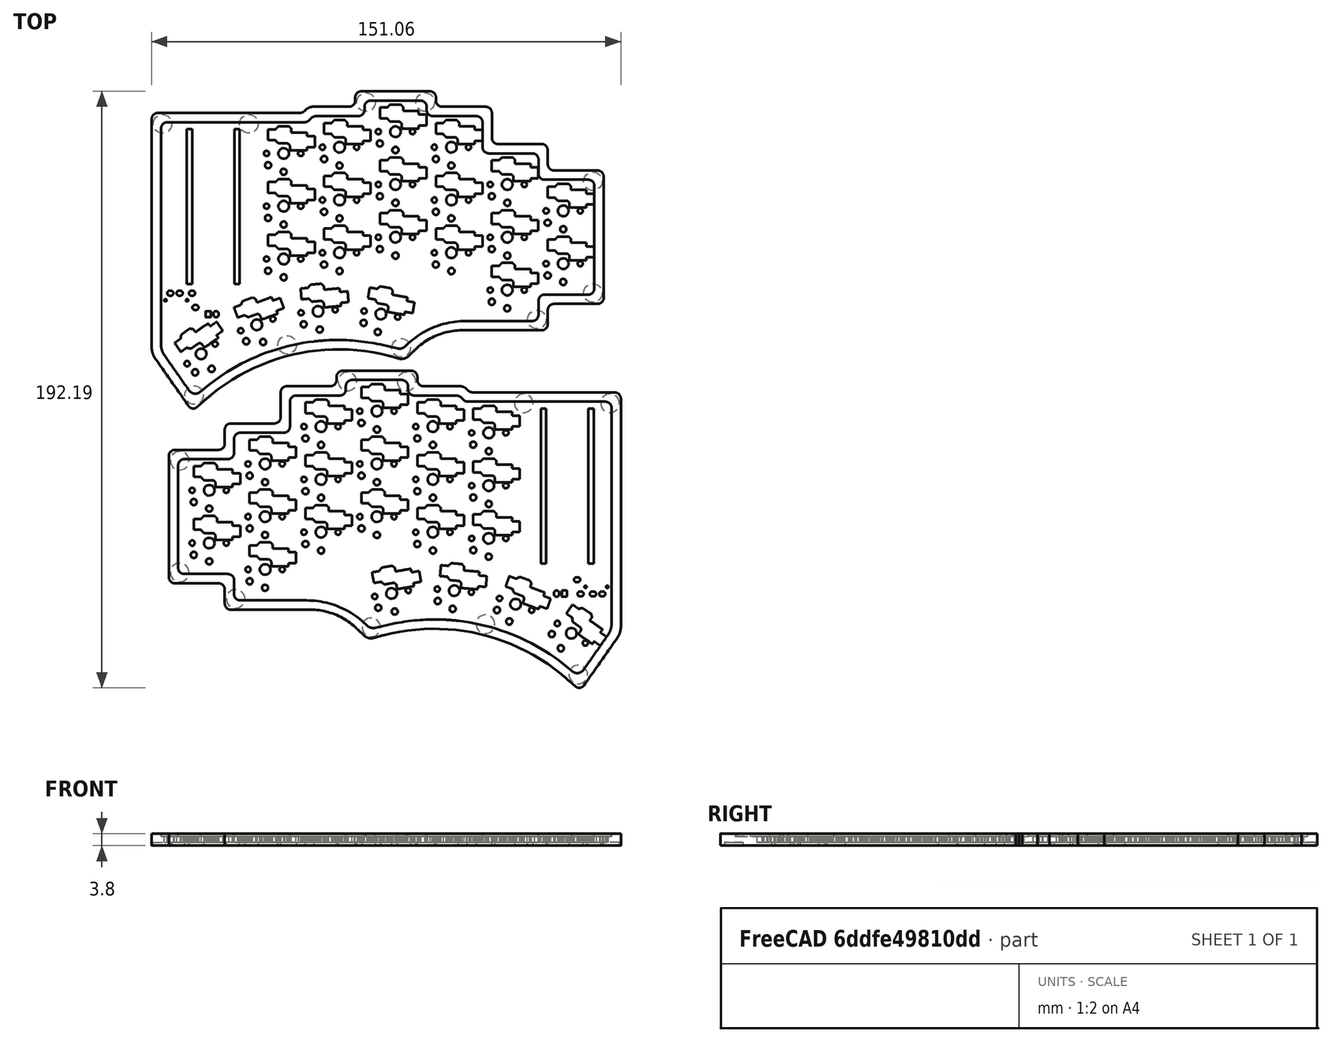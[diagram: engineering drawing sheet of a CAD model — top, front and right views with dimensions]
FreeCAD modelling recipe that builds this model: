
FCSTD DOCUMENT  (FreeCAD 0.21R33771 (Git))
Label: case
License: All rights reserved
LicenseURL: http://en.wikipedia.org/wiki/All_rights_reserved
objects: Part::Feature×296, Part::Extrusion×296, Part::MultiFuse×4, Part::FeaturePython×2, Part::Mirroring×1
note: 599 computed .brp shape members not serialized (recipe doc carries the construction recipe); baked Part::Feature solids carry a one-line shape summary decoded from their .brp

FEATURE [Part::Feature] path44149_5_3
  shape: bbox 145.5 x 102.4 x 2e-07 mm, 0 faces, 0 solids (baked)
FEATURE [Part::Extrusion] Extrude  label="bounds_left"
  Base = -> path44149_5_3
  Dir = (0,0,1)
  DirMode = 0
  FaceMakerClass = Part::FaceMakerBullseye
  LengthFwd = 3.8
  LengthRev = 0
  Solid = true
  Symmetric = false
FEATURE [Part::Feature] path44149_5_1
  shape: bbox 139.5 x 94.73 x 2e-07 mm, 0 faces, 0 solids (baked)
FEATURE [Part::Extrusion] Extrude001  label="inner_left"
  Base = -> path44149_5_1
  Dir = (0,0,1)
  DirMode = 0
  FaceMakerClass = Part::FaceMakerBullseye
  LengthFwd = 0.8
  LengthRev = 0
  Placement = pos=(0,0,3) rot=(0,0,1;0rad)
  Solid = true
  Symmetric = false
FEATURE [Part::Feature] path9
  Placement = pos=(71.4721,-85.7664,0) rot=(0,0,1;0rad)
  shape: bbox 6.624 x 7.244 x 2e-07 mm, 0 faces, 0 solids (baked)
FEATURE [Part::Feature] path9_9
  Placement = pos=(71.4721,-121.766,0) rot=(0,0,1;0rad)
  shape: bbox 6.624 x 7.244 x 2e-07 mm, 0 faces, 0 solids (baked)
FEATURE [Part::Feature] path9_92_7_9
  Placement = pos=(125.472,-60.2664,0) rot=(0,0,1;0rad)
  shape: bbox 6.624 x 7.244 x 2e-07 mm, 0 faces, 0 solids (baked)
FEATURE [Part::Feature] path9_92_7_9_9
  Placement = pos=(144.472,-60.2664,0) rot=(0,0,1;0rad)
  shape: bbox 6.624 x 7.244 x 2e-07 mm, 0 faces, 0 solids (baked)
FEATURE [Part::Feature] path9_92_7_9_9_4
  Placement = pos=(210.001,-67.2664,0) rot=(0,0,1;0rad)
  shape: bbox 6.624 x 7.244 x 2e-07 mm, 0 faces, 0 solids (baked)
FEATURE [Part::Feature] path9_9_5
  Placement = pos=(89.4721,-130.266,0) rot=(0,0,1;0rad)
  shape: bbox 6.624 x 7.244 x 2e-07 mm, 0 faces, 0 solids (baked)
FEATURE [Part::Feature] path9_92_7_9_9_4_4_8_2
  Placement = pos=(199.796,-154.63,0) rot=(0,0,1;0rad)
  shape: bbox 6.624 x 7.244 x 2e-07 mm, 0 faces, 0 solids (baked)
FEATURE [Part::Feature] path9_92_7_9_9_4_4_8_2_4
  Placement = pos=(133.155,-139.413,0) rot=(0,0,1;0rad)
  shape: bbox 6.624 x 7.244 x 2e-07 mm, 0 faces, 0 solids (baked)
FEATURE [Part::Feature] path9_92_7_9_9_4_4_8_2_4_6
  Placement = pos=(169.885,-138.433,0) rot=(0,0,1;0rad)
  shape: bbox 6.624 x 7.244 x 2e-07 mm, 0 faces, 0 solids (baked)
FEATURE [Part::Feature] path9_92_7_9_9_4_4_8_2_4_0
  Placement = pos=(182.228,-67.2664,0) rot=(0,0,1;0rad)
  shape: bbox 6.624 x 7.244 x 2e-07 mm, 0 faces, 0 solids (baked)
FEATURE [Part::Extrusion] Extrude002
  Base = -> path9
  Dir = (0,0,1)
  DirMode = 0
  FaceMakerClass = Part::FaceMakerBullseye
  LengthFwd = 1
  LengthRev = 0
  Solid = true
  Symmetric = false
FEATURE [Part::Extrusion] Extrude003
  Base = -> path9_9
  Dir = (0,0,1)
  DirMode = 0
  FaceMakerClass = Part::FaceMakerBullseye
  LengthFwd = 1
  LengthRev = 0
  Solid = true
  Symmetric = false
FEATURE [Part::Extrusion] Extrude004
  Base = -> path9_92_7_9
  Dir = (0,0,1)
  DirMode = 0
  FaceMakerClass = Part::FaceMakerBullseye
  LengthFwd = 1
  LengthRev = 0
  Solid = true
  Symmetric = false
FEATURE [Part::Extrusion] Extrude005
  Base = -> path9_92_7_9_9
  Dir = (0,0,1)
  DirMode = 0
  FaceMakerClass = Part::FaceMakerBullseye
  LengthFwd = 1
  LengthRev = 0
  Solid = true
  Symmetric = false
FEATURE [Part::Extrusion] Extrude006
  Base = -> path9_92_7_9_9_4
  Dir = (0,0,1)
  DirMode = 0
  FaceMakerClass = Part::FaceMakerBullseye
  LengthFwd = 1
  LengthRev = 0
  Solid = true
  Symmetric = false
FEATURE [Part::Extrusion] Extrude007
  Base = -> path9_9_5
  Dir = (0,0,1)
  DirMode = 0
  FaceMakerClass = Part::FaceMakerBullseye
  LengthFwd = 1
  LengthRev = 0
  Solid = true
  Symmetric = false
FEATURE [Part::Extrusion] Extrude008
  Base = -> path9_92_7_9_9_4_4_8_2
  Dir = (0,0,1)
  DirMode = 0
  FaceMakerClass = Part::FaceMakerBullseye
  LengthFwd = 1
  LengthRev = 0
  Solid = true
  Symmetric = false
FEATURE [Part::Extrusion] Extrude009
  Base = -> path9_92_7_9_9_4_4_8_2_4
  Dir = (0,0,1)
  DirMode = 0
  FaceMakerClass = Part::FaceMakerBullseye
  LengthFwd = 1
  LengthRev = 0
  Solid = true
  Symmetric = false
FEATURE [Part::Extrusion] Extrude010
  Base = -> path9_92_7_9_9_4_4_8_2_4_6
  Dir = (0,0,1)
  DirMode = 0
  FaceMakerClass = Part::FaceMakerBullseye
  LengthFwd = 1
  LengthRev = 0
  Solid = true
  Symmetric = false
FEATURE [Part::Extrusion] Extrude011
  Base = -> path9_92_7_9_9_4_4_8_2_4_0
  Dir = (0,0,1)
  DirMode = 0
  FaceMakerClass = Part::FaceMakerBullseye
  LengthFwd = 1
  LengthRev = 0
  Solid = true
  Symmetric = false
FEATURE [Part::MultiFuse] Fusion  label="feet_left"
  Shapes = -> [Extrude002,Extrude003,Extrude004,Extrude005,Extrude006,Extrude007,Extrude008,Extrude009,Extrude010,Extrude011]
FEATURE [Part::Feature] path61609_4_5_7_9_4_80_0_5
  shape: bbox 15 x 7.701 x 2e-07 mm, 0 faces, 0 solids (baked)
FEATURE [Part::Feature] path61609_4_5_7_9_4_80_0_3_2
  shape: bbox 15 x 7.701 x 2e-07 mm, 0 faces, 0 solids (baked)
FEATURE [Part::Feature] path52377_09_3_1_8_87
  Placement = pos=(40.6315,-49.1329,0) rot=(0,0,1;0rad)
  shape: bbox 1.877 x 2.052 x 2e-07 mm, 0 faces, 0 solids (baked)
FEATURE [Part::Feature] path52401_71_2_4_9_8
  Placement = pos=(41.1315,-52.9329,0) rot=(0,0,1;0rad)
  shape: bbox 2.208 x 2.415 x 2e-07 mm, 0 faces, 0 solids (baked)
FEATURE [Part::Feature] path52401_7_8_1_8_2_30
  Placement = pos=(46.1315,-55.0329,0) rot=(0,0,1;0rad)
  shape: bbox 2.208 x 2.415 x 2e-07 mm, 0 faces, 0 solids (baked)
FEATURE [Part::Feature] path52377_0_5_0_4_2_3
  Placement = pos=(51.6315,-49.1329,0) rot=(0,0,1;0rad)
  shape: bbox 1.877 x 2.052 x 2e-07 mm, 0 faces, 0 solids (baked)
FEATURE [Part::Feature] path52456_0_5_5_7_86
  Placement = pos=(46.1315,-49.1329,0) rot=(0,0,1;0rad)
  shape: bbox 3.787 x 4.141 x 2e-07 mm, 0 faces, 0 solids (baked)
FEATURE [Part::Feature] path52377_09_3_1_8_8_2
  Placement = pos=(40.6315,-49.1329,0) rot=(0,0,1;0rad)
  shape: bbox 1.877 x 2.052 x 2e-07 mm, 0 faces, 0 solids (baked)
FEATURE [Part::Feature] path52401_71_2_4_9_4_5
  Placement = pos=(41.1315,-52.9329,0) rot=(0,0,1;0rad)
  shape: bbox 2.208 x 2.415 x 2e-07 mm, 0 faces, 0 solids (baked)
FEATURE [Part::Feature] path52401_7_8_1_8_2_3_11
  Placement = pos=(46.1315,-55.0329,0) rot=(0,0,1;0rad)
  shape: bbox 2.208 x 2.415 x 2e-07 mm, 0 faces, 0 solids (baked)
FEATURE [Part::Feature] path52377_0_5_0_4_2_4_5
  Placement = pos=(51.6315,-49.1329,0) rot=(0,0,1;0rad)
  shape: bbox 1.877 x 2.052 x 2e-07 mm, 0 faces, 0 solids (baked)
FEATURE [Part::Feature] path52456_0_5_5_7_7_0
  Placement = pos=(46.1315,-49.1329,0) rot=(0,0,1;0rad)
  shape: bbox 3.787 x 4.141 x 2e-07 mm, 0 faces, 0 solids (baked)
FEATURE [Part::Feature] path52377_09_3_1_8_2_3
  Placement = pos=(40.6315,-49.1329,0) rot=(0,0,1;0rad)
  shape: bbox 1.877 x 2.052 x 2e-07 mm, 0 faces, 0 solids (baked)
FEATURE [Part::Feature] path52401_71_2_4_9_2_39
  Placement = pos=(41.1315,-52.9329,0) rot=(0,0,1;0rad)
  shape: bbox 2.208 x 2.415 x 2e-07 mm, 0 faces, 0 solids (baked)
FEATURE [Part::Feature] path52401_7_8_1_8_2_31_2
  Placement = pos=(46.1315,-55.0329,0) rot=(0,0,1;0rad)
  shape: bbox 2.208 x 2.415 x 2e-07 mm, 0 faces, 0 solids (baked)
FEATURE [Part::Feature] path52377_0_5_0_4_2_41_1
  Placement = pos=(51.6315,-49.1329,0) rot=(0,0,1;0rad)
  shape: bbox 1.877 x 2.052 x 2e-07 mm, 0 faces, 0 solids (baked)
FEATURE [Part::Feature] path52456_0_5_5_7_4_2
  Placement = pos=(46.1315,-49.1329,0) rot=(0,0,1;0rad)
  shape: bbox 3.787 x 4.141 x 2e-07 mm, 0 faces, 0 solids (baked)
FEATURE [Part::Feature] path52377_09_3_1_8_2_4_7
  Placement = pos=(40.6315,-49.1329,0) rot=(0,0,1;0rad)
  shape: bbox 1.877 x 2.052 x 2e-07 mm, 0 faces, 0 solids (baked)
FEATURE [Part::Feature] path52401_71_2_4_9_2_9_8
  Placement = pos=(41.1315,-52.9329,0) rot=(0,0,1;0rad)
  shape: bbox 2.208 x 2.415 x 2e-07 mm, 0 faces, 0 solids (baked)
FEATURE [Part::Feature] path52401_7_8_1_8_2_31_5_4
  Placement = pos=(46.1315,-55.0329,0) rot=(0,0,1;0rad)
  shape: bbox 2.208 x 2.415 x 2e-07 mm, 0 faces, 0 solids (baked)
FEATURE [Part::Feature] path52377_0_5_0_4_2_41_0_0
  Placement = pos=(51.6315,-49.1329,0) rot=(0,0,1;0rad)
  shape: bbox 1.877 x 2.052 x 2e-07 mm, 0 faces, 0 solids (baked)
FEATURE [Part::Feature] path52456_0_5_5_7_4_4_1
  Placement = pos=(46.1315,-49.1329,0) rot=(0,0,1;0rad)
  shape: bbox 3.787 x 4.141 x 2e-07 mm, 0 faces, 0 solids (baked)
FEATURE [Part::Feature] path52377_09_3_1_8_8_0_3
  Placement = pos=(40.6315,-49.1329,0) rot=(0,0,1;0rad)
  shape: bbox 1.877 x 2.052 x 2e-07 mm, 0 faces, 0 solids (baked)
FEATURE [Part::Feature] path52401_71_2_4_9_4_2_0
  Placement = pos=(41.1315,-52.9329,0) rot=(0,0,1;0rad)
  shape: bbox 2.208 x 2.415 x 2e-07 mm, 0 faces, 0 solids (baked)
FEATURE [Part::Feature] path52401_7_8_1_8_2_3_5_0
  Placement = pos=(46.1315,-55.0329,0) rot=(0,0,1;0rad)
  shape: bbox 2.208 x 2.415 x 2e-07 mm, 0 faces, 0 solids (baked)
FEATURE [Part::Feature] path52377_0_5_0_4_2_4_4_3
  Placement = pos=(51.6315,-49.1329,0) rot=(0,0,1;0rad)
  shape: bbox 1.877 x 2.052 x 2e-07 mm, 0 faces, 0 solids (baked)
FEATURE [Part::Feature] path52456_0_5_5_7_7_7_7
  Placement = pos=(46.1315,-49.1329,0) rot=(0,0,1;0rad)
  shape: bbox 3.787 x 4.141 x 2e-07 mm, 0 faces, 0 solids (baked)
FEATURE [Part::Feature] path52377_09_3_1_8_2_9_7
  Placement = pos=(40.6315,-49.1329,0) rot=(0,0,1;0rad)
  shape: bbox 1.877 x 2.052 x 2e-07 mm, 0 faces, 0 solids (baked)
FEATURE [Part::Feature] path52401_71_2_4_9_2_6_0
  Placement = pos=(41.1315,-52.9329,0) rot=(0,0,1;0rad)
  shape: bbox 2.208 x 2.415 x 2e-07 mm, 0 faces, 0 solids (baked)
FEATURE [Part::Feature] path52401_7_8_1_8_2_31_56_74
  Placement = pos=(46.1315,-55.0329,0) rot=(0,0,1;0rad)
  shape: bbox 2.208 x 2.415 x 2e-07 mm, 0 faces, 0 solids (baked)
FEATURE [Part::Feature] path52377_0_5_0_4_2_41_4_91
  Placement = pos=(51.6315,-49.1329,0) rot=(0,0,1;0rad)
  shape: bbox 1.877 x 2.052 x 2e-07 mm, 0 faces, 0 solids (baked)
FEATURE [Part::Feature] path52456_0_5_5_7_4_40_0
  Placement = pos=(46.1315,-49.1329,0) rot=(0,0,1;0rad)
  shape: bbox 3.787 x 4.141 x 2e-07 mm, 0 faces, 0 solids (baked)
FEATURE [Part::Feature] path52377_09_3_1_8_2_4_0_1
  Placement = pos=(40.6315,-49.1329,0) rot=(0,0,1;0rad)
  shape: bbox 1.877 x 2.052 x 2e-07 mm, 0 faces, 0 solids (baked)
FEATURE [Part::Feature] path52401_71_2_4_9_2_9_9_55
  Placement = pos=(41.1315,-52.9329,0) rot=(0,0,1;0rad)
  shape: bbox 2.208 x 2.415 x 2e-07 mm, 0 faces, 0 solids (baked)
FEATURE [Part::Feature] path52401_7_8_1_8_2_31_5_9_4
  Placement = pos=(46.1315,-55.0329,0) rot=(0,0,1;0rad)
  shape: bbox 2.208 x 2.415 x 2e-07 mm, 0 faces, 0 solids (baked)
FEATURE [Part::Feature] path52377_0_5_0_4_2_41_0_4_8
  Placement = pos=(51.6315,-49.1329,0) rot=(0,0,1;0rad)
  shape: bbox 1.877 x 2.052 x 2e-07 mm, 0 faces, 0 solids (baked)
FEATURE [Part::Feature] path52456_0_5_5_7_4_4_8_02
  Placement = pos=(46.1315,-49.1329,0) rot=(0,0,1;0rad)
  shape: bbox 3.787 x 4.141 x 2e-07 mm, 0 faces, 0 solids (baked)
FEATURE [Part::Feature] path52377_09_3_1_8_8_0_4_7
  Placement = pos=(40.6315,-49.1329,0) rot=(0,0,1;0rad)
  shape: bbox 1.877 x 2.052 x 2e-07 mm, 0 faces, 0 solids (baked)
FEATURE [Part::Feature] path52401_71_2_4_9_4_2_2_1
  Placement = pos=(41.1315,-52.9329,0) rot=(0,0,1;0rad)
  shape: bbox 2.208 x 2.415 x 2e-07 mm, 0 faces, 0 solids (baked)
FEATURE [Part::Feature] path52401_7_8_1_8_2_3_5_3_8
  Placement = pos=(46.1315,-55.0329,0) rot=(0,0,1;0rad)
  shape: bbox 2.208 x 2.415 x 2e-07 mm, 0 faces, 0 solids (baked)
FEATURE [Part::Feature] path52377_0_5_0_4_2_4_4_8_3
  Placement = pos=(51.6315,-49.1329,0) rot=(0,0,1;0rad)
  shape: bbox 1.877 x 2.052 x 2e-07 mm, 0 faces, 0 solids (baked)
FEATURE [Part::Feature] path52456_0_5_5_7_7_7_1_3
  Placement = pos=(46.1315,-49.1329,0) rot=(0,0,1;0rad)
  shape: bbox 3.787 x 4.141 x 2e-07 mm, 0 faces, 0 solids (baked)
FEATURE [Part::Feature] path52377_09_3_1_8_2_9_5_3
  Placement = pos=(40.6315,-49.1329,0) rot=(0,0,1;0rad)
  shape: bbox 1.877 x 2.052 x 2e-07 mm, 0 faces, 0 solids (baked)
FEATURE [Part::Feature] path52401_71_2_4_9_2_6_3_64
  Placement = pos=(41.1315,-52.9329,0) rot=(0,0,1;0rad)
  shape: bbox 2.208 x 2.415 x 2e-07 mm, 0 faces, 0 solids (baked)
FEATURE [Part::Feature] path52401_7_8_1_8_2_31_56_1_9
  Placement = pos=(46.1315,-55.0329,0) rot=(0,0,1;0rad)
  shape: bbox 2.208 x 2.415 x 2e-07 mm, 0 faces, 0 solids (baked)
FEATURE [Part::Feature] path52377_0_5_0_4_2_41_4_8_1
  Placement = pos=(51.6315,-49.1329,0) rot=(0,0,1;0rad)
  shape: bbox 1.877 x 2.052 x 2e-07 mm, 0 faces, 0 solids (baked)
FEATURE [Part::Feature] path52456_0_5_5_7_4_40_5_0
  Placement = pos=(46.1315,-49.1329,0) rot=(0,0,1;0rad)
  shape: bbox 3.787 x 4.141 x 2e-07 mm, 0 faces, 0 solids (baked)
FEATURE [Part::Feature] path52377_09_3_1_8_2_4_0_5_8
  Placement = pos=(40.6315,-49.1329,0) rot=(0,0,1;0rad)
  shape: bbox 1.877 x 2.052 x 2e-07 mm, 0 faces, 0 solids (baked)
FEATURE [Part::Feature] path52401_71_2_4_9_2_9_9_5_64
  Placement = pos=(41.1315,-52.9329,0) rot=(0,0,1;0rad)
  shape: bbox 2.208 x 2.415 x 2e-07 mm, 0 faces, 0 solids (baked)
FEATURE [Part::Feature] path52401_7_8_1_8_2_31_5_9_9_9
  Placement = pos=(46.1315,-55.0329,0) rot=(0,0,1;0rad)
  shape: bbox 2.208 x 2.415 x 2e-07 mm, 0 faces, 0 solids (baked)
FEATURE [Part::Feature] path52377_0_5_0_4_2_41_0_4_1_4
  Placement = pos=(51.6315,-49.1329,0) rot=(0,0,1;0rad)
  shape: bbox 1.877 x 2.052 x 2e-07 mm, 0 faces, 0 solids (baked)
FEATURE [Part::Feature] path52456_0_5_5_7_4_4_8_5_4
  Placement = pos=(46.1315,-49.1329,0) rot=(0,0,1;0rad)
  shape: bbox 3.787 x 4.141 x 2e-07 mm, 0 faces, 0 solids (baked)
FEATURE [Part::Feature] path52377_09_3_1_8_8_0_4_5_6
  Placement = pos=(40.6315,-49.1329,0) rot=(0,0,1;0rad)
  shape: bbox 1.877 x 2.052 x 2e-07 mm, 0 faces, 0 solids (baked)
FEATURE [Part::Feature] path52401_71_2_4_9_4_2_2_8_5
  Placement = pos=(41.1315,-52.9329,0) rot=(0,0,1;0rad)
  shape: bbox 2.208 x 2.415 x 2e-07 mm, 0 faces, 0 solids (baked)
FEATURE [Part::Feature] path52401_7_8_1_8_2_3_5_3_4_2
  Placement = pos=(46.1315,-55.0329,0) rot=(0,0,1;0rad)
  shape: bbox 2.208 x 2.415 x 2e-07 mm, 0 faces, 0 solids (baked)
FEATURE [Part::Feature] path52377_0_5_0_4_2_4_4_8_9_1
  Placement = pos=(51.6315,-49.1329,0) rot=(0,0,1;0rad)
  shape: bbox 1.877 x 2.052 x 2e-07 mm, 0 faces, 0 solids (baked)
FEATURE [Part::Feature] path52456_0_5_5_7_7_7_1_7_8
  Placement = pos=(46.1315,-49.1329,0) rot=(0,0,1;0rad)
  shape: bbox 3.787 x 4.141 x 2e-07 mm, 0 faces, 0 solids (baked)
FEATURE [Part::Feature] path52377_09_3_1_8_2_9_5_4_8
  Placement = pos=(40.6315,-49.1329,0) rot=(0,0,1;0rad)
  shape: bbox 1.877 x 2.052 x 2e-07 mm, 0 faces, 0 solids (baked)
FEATURE [Part::Feature] path52401_71_2_4_9_2_6_3_6_9
  Placement = pos=(41.1315,-52.9329,0) rot=(0,0,1;0rad)
  shape: bbox 2.208 x 2.415 x 2e-07 mm, 0 faces, 0 solids (baked)
FEATURE [Part::Feature] path52401_7_8_1_8_2_31_56_1_3_7
  Placement = pos=(46.1315,-55.0329,0) rot=(0,0,1;0rad)
  shape: bbox 2.208 x 2.415 x 2e-07 mm, 0 faces, 0 solids (baked)
FEATURE [Part::Feature] path52377_0_5_0_4_2_41_4_8_8_6
  Placement = pos=(51.6315,-49.1329,0) rot=(0,0,1;0rad)
  shape: bbox 1.877 x 2.052 x 2e-07 mm, 0 faces, 0 solids (baked)
FEATURE [Part::Feature] path52456_0_5_5_7_4_40_5_1_45
  Placement = pos=(46.1315,-49.1329,0) rot=(0,0,1;0rad)
  shape: bbox 3.787 x 4.141 x 2e-07 mm, 0 faces, 0 solids (baked)
FEATURE [Part::Feature] path52377_09_3_1_8_2_4_0_5_0_4
  Placement = pos=(40.6315,-49.1329,0) rot=(0,0,1;0rad)
  shape: bbox 1.877 x 2.052 x 2e-07 mm, 0 faces, 0 solids (baked)
FEATURE [Part::Feature] path52401_71_2_4_9_2_9_9_5_6_8
  Placement = pos=(41.1315,-52.9329,0) rot=(0,0,1;0rad)
  shape: bbox 2.208 x 2.415 x 2e-07 mm, 0 faces, 0 solids (baked)
FEATURE [Part::Feature] path52401_7_8_1_8_2_31_5_9_9_0_0
  Placement = pos=(46.1315,-55.0329,0) rot=(0,0,1;0rad)
  shape: bbox 2.208 x 2.415 x 2e-07 mm, 0 faces, 0 solids (baked)
FEATURE [Part::Feature] path52377_0_5_0_4_2_41_0_4_1_8_44
  Placement = pos=(51.6315,-49.1329,0) rot=(0,0,1;0rad)
  shape: bbox 1.877 x 2.052 x 2e-07 mm, 0 faces, 0 solids (baked)
FEATURE [Part::Feature] path52456_0_5_5_7_4_4_8_5_8_8
  Placement = pos=(46.1315,-49.1329,0) rot=(0,0,1;0rad)
  shape: bbox 3.787 x 4.141 x 2e-07 mm, 0 faces, 0 solids (baked)
FEATURE [Part::Feature] path52377_09_3_1_8_8_0_4_5_8_91
  Placement = pos=(40.6315,-49.1329,0) rot=(0,0,1;0rad)
  shape: bbox 1.877 x 2.052 x 2e-07 mm, 0 faces, 0 solids (baked)
FEATURE [Part::Feature] path52401_71_2_4_9_4_2_2_8_7_5
  Placement = pos=(41.1315,-52.9329,0) rot=(0,0,1;0rad)
  shape: bbox 2.208 x 2.415 x 2e-07 mm, 0 faces, 0 solids (baked)
FEATURE [Part::Feature] path52401_7_8_1_8_2_3_5_3_4_4_44
  Placement = pos=(46.1315,-55.0329,0) rot=(0,0,1;0rad)
  shape: bbox 2.208 x 2.415 x 2e-07 mm, 0 faces, 0 solids (baked)
FEATURE [Part::Feature] path52377_0_5_0_4_2_4_4_8_9_2_9
  Placement = pos=(51.6315,-49.1329,0) rot=(0,0,1;0rad)
  shape: bbox 1.877 x 2.052 x 2e-07 mm, 0 faces, 0 solids (baked)
FEATURE [Part::Feature] path52456_0_5_5_7_7_7_1_7_0_2
  Placement = pos=(46.1315,-49.1329,0) rot=(0,0,1;0rad)
  shape: bbox 3.787 x 4.141 x 2e-07 mm, 0 faces, 0 solids (baked)
FEATURE [Part::Feature] path52377_09_3_1_8_2_9_5_4_9_5
  Placement = pos=(40.6315,-49.1329,0) rot=(0,0,1;0rad)
  shape: bbox 1.877 x 2.052 x 2e-07 mm, 0 faces, 0 solids (baked)
FEATURE [Part::Feature] path52401_71_2_4_9_2_6_3_6_8_5
  Placement = pos=(41.1315,-52.9329,0) rot=(0,0,1;0rad)
  shape: bbox 2.208 x 2.415 x 2e-07 mm, 0 faces, 0 solids (baked)
FEATURE [Part::Feature] path52401_7_8_1_8_2_31_56_1_3_0_2
  Placement = pos=(46.1315,-55.0329,0) rot=(0,0,1;0rad)
  shape: bbox 2.208 x 2.415 x 2e-07 mm, 0 faces, 0 solids (baked)
FEATURE [Part::Feature] path52377_0_5_0_4_2_41_4_8_8_0_5
  Placement = pos=(51.6315,-49.1329,0) rot=(0,0,1;0rad)
  shape: bbox 1.877 x 2.052 x 2e-07 mm, 0 faces, 0 solids (baked)
FEATURE [Part::Feature] path52456_0_5_5_7_4_40_5_1_5_56
  Placement = pos=(46.1315,-49.1329,0) rot=(0,0,1;0rad)
  shape: bbox 3.787 x 4.141 x 2e-07 mm, 0 faces, 0 solids (baked)
FEATURE [Part::Feature] path52377_09_3_1_8_2_4_0_5_0_2_7
  Placement = pos=(40.6315,-49.1329,0) rot=(0,0,1;0rad)
  shape: bbox 1.877 x 2.052 x 2e-07 mm, 0 faces, 0 solids (baked)
FEATURE [Part::Feature] path52401_71_2_4_9_2_9_9_5_6_2_6
  Placement = pos=(41.1315,-52.9329,0) rot=(0,0,1;0rad)
  shape: bbox 2.208 x 2.415 x 2e-07 mm, 0 faces, 0 solids (baked)
FEATURE [Part::Feature] path52401_7_8_1_8_2_31_5_9_9_0_7_2
  Placement = pos=(46.1315,-55.0329,0) rot=(0,0,1;0rad)
  shape: bbox 2.208 x 2.415 x 2e-07 mm, 0 faces, 0 solids (baked)
FEATURE [Part::Feature] path52377_0_5_0_4_2_41_0_4_1_8_4_4
  Placement = pos=(51.6315,-49.1329,0) rot=(0,0,1;0rad)
  shape: bbox 1.877 x 2.052 x 2e-07 mm, 0 faces, 0 solids (baked)
FEATURE [Part::Feature] path52456_0_5_5_7_4_4_8_5_8_0_3
  Placement = pos=(46.1315,-49.1329,0) rot=(0,0,1;0rad)
  shape: bbox 3.787 x 4.141 x 2e-07 mm, 0 faces, 0 solids (baked)
FEATURE [Part::Feature] path52377_09_3_1_8_8_0_4_5_8_9_1
  Placement = pos=(40.6315,-49.1329,0) rot=(0,0,1;0rad)
  shape: bbox 1.877 x 2.052 x 2e-07 mm, 0 faces, 0 solids (baked)
FEATURE [Part::Feature] path52401_71_2_4_9_4_2_2_8_7_6_2
  Placement = pos=(41.1315,-52.9329,0) rot=(0,0,1;0rad)
  shape: bbox 2.208 x 2.415 x 2e-07 mm, 0 faces, 0 solids (baked)
FEATURE [Part::Feature] path52401_7_8_1_8_2_3_5_3_4_4_8_8
  Placement = pos=(46.1315,-55.0329,0) rot=(0,0,1;0rad)
  shape: bbox 2.208 x 2.415 x 2e-07 mm, 0 faces, 0 solids (baked)
FEATURE [Part::Feature] path52377_0_5_0_4_2_4_4_8_9_2_0_5
  Placement = pos=(51.6315,-49.1329,0) rot=(0,0,1;0rad)
  shape: bbox 1.877 x 2.052 x 2e-07 mm, 0 faces, 0 solids (baked)
FEATURE [Part::Feature] path52456_0_5_5_7_7_7_1_7_0_0_6
  Placement = pos=(46.1315,-49.1329,0) rot=(0,0,1;0rad)
  shape: bbox 3.787 x 4.141 x 2e-07 mm, 0 faces, 0 solids (baked)
FEATURE [Part::Feature] circle37307_9_0_7_1
  Placement = pos=(138.24,-66.7421,0) rot=(0,0,1;0rad)
  shape: bbox 0.8832 x 0.9658 x 2e-07 mm, 0 faces, 0 solids (baked)
FEATURE [Part::Feature] circle37313_0_5_2_6
  Placement = pos=(131.24,-66.7421,0) rot=(0,0,1;0rad)
  shape: bbox 0.8832 x 0.9658 x 2e-07 mm, 0 faces, 0 solids (baked)
FEATURE [Part::Feature] path8_2
  shape: bbox 2.002 x 1.601 x 2e-07 mm, 0 faces, 0 solids (baked)
FEATURE [Part::Feature] path4_1
  shape: bbox 2.002 x 1.601 x 2e-07 mm, 0 faces, 0 solids (baked)
FEATURE [Part::Feature] path6_5
  shape: bbox 2.002 x 1.601 x 2e-07 mm, 0 faces, 0 solids (baked)
FEATURE [Part::Feature] path2_5
  shape: bbox 2.002 x 1.601 x 2e-07 mm, 0 faces, 0 solids (baked)
FEATURE [Part::Feature] path37931_6_3_3
  shape: bbox 1.7 x 2 x 2e-07 mm, 0 faces, 0 solids (baked)
FEATURE [Part::Feature] path37937_8_1_8
  shape: bbox 1.702 x 2 x 2e-07 mm, 0 faces, 0 solids (baked)
FEATURE [Part::Feature] rect117948_1_5_1_8
  shape: bbox 1.7 x 49.96 x 2e-07 mm, 0 faces, 0 solids (baked)
FEATURE [Part::Feature] rect117948_2_0_8_5_8
  shape: bbox 1.7 x 49.96 x 2e-07 mm, 0 faces, 0 solids (baked)
FEATURE [Part::Feature] path61609_4_5_7_9_4_80_0_8_78
  shape: bbox 15 x 7.701 x 2e-07 mm, 0 faces, 0 solids (baked)
FEATURE [Part::Feature] path61609_4_5_7_9_4_80_0_3_8_68
  shape: bbox 15 x 7.701 x 2e-07 mm, 0 faces, 0 solids (baked)
FEATURE [Part::Feature] path61609_4_5_7_9_4_80_0_3_8_6_79
  shape: bbox 15 x 7.701 x 2e-07 mm, 0 faces, 0 solids (baked)
FEATURE [Part::Feature] path61609_4_5_7_9_4_80_0_8_3_5
  shape: bbox 15 x 7.701 x 2e-07 mm, 0 faces, 0 solids (baked)
FEATURE [Part::Feature] path61609_4_5_7_9_4_80_0_3_8_9_3
  shape: bbox 15 x 7.701 x 2e-07 mm, 0 faces, 0 solids (baked)
FEATURE [Part::Feature] path61609_4_5_7_9_4_80_0_3_8_6_1_2
  shape: bbox 15 x 7.701 x 2e-07 mm, 0 faces, 0 solids (baked)
FEATURE [Part::Feature] path61609_4_5_7_9_4_80_0_8_7_0
  shape: bbox 15 x 7.701 x 2e-07 mm, 0 faces, 0 solids (baked)
FEATURE [Part::Feature] path61609_4_5_7_9_4_80_0_3_8_91_1
  shape: bbox 15 x 7.701 x 2e-07 mm, 0 faces, 0 solids (baked)
FEATURE [Part::Feature] path61609_4_5_7_9_4_80_0_3_8_6_3_6
  shape: bbox 15 x 7.701 x 2e-07 mm, 0 faces, 0 solids (baked)
FEATURE [Part::Feature] path61609_4_5_7_9_4_80_0_8_8_6
  shape: bbox 15 x 7.701 x 2e-07 mm, 0 faces, 0 solids (baked)
FEATURE [Part::Feature] path61609_4_5_7_9_4_80_0_3_8_0_9
  shape: bbox 15 x 7.701 x 2e-07 mm, 0 faces, 0 solids (baked)
FEATURE [Part::Feature] path61609_4_5_7_9_4_80_0_3_8_6_7_8
  shape: bbox 15 x 7.701 x 2e-07 mm, 0 faces, 0 solids (baked)
FEATURE [Part::Feature] path61609_4_5_7_9_4_80_0_8_2_6
  shape: bbox 15 x 7.701 x 2e-07 mm, 0 faces, 0 solids (baked)
FEATURE [Part::Feature] path61609_4_5_7_9_4_80_0_3_8_60_6
  shape: bbox 15 x 7.701 x 2e-07 mm, 0 faces, 0 solids (baked)
FEATURE [Part::Feature] path61609_4_5_7_9_4_80_0_3_8_6_4_2
  shape: bbox 15 x 7.701 x 2e-07 mm, 0 faces, 0 solids (baked)
FEATURE [Part::Feature] path52377_09_3_5_7_6_7_3_2
  Placement = pos=(40.6315,-49.1329,0) rot=(0,0,1;0rad)
  shape: bbox 2.046 x 1.998 x 2e-07 mm, 0 faces, 0 solids (baked)
FEATURE [Part::Feature] path52401_71_2_5_9_2_77_3_4
  Placement = pos=(41.1315,-52.9329,0) rot=(0,0,1;0rad)
  shape: bbox 2.407 x 2.351 x 2e-07 mm, 0 faces, 0 solids (baked)
FEATURE [Part::Feature] path52401_7_8_1_1_7_3_9_0_7
  Placement = pos=(46.1315,-55.0329,0) rot=(0,0,1;0rad)
  shape: bbox 2.407 x 2.351 x 2e-07 mm, 0 faces, 0 solids (baked)
FEATURE [Part::Feature] path52377_0_5_0_1_9_1_5_5_6
  Placement = pos=(51.6315,-49.1329,0) rot=(0,0,1;0rad)
  shape: bbox 2.046 x 1.998 x 2e-07 mm, 0 faces, 0 solids (baked)
FEATURE [Part::Feature] path52456_0_5_2_2_2_3_5_8
  Placement = pos=(46.1315,-49.1329,0) rot=(0,0,1;0rad)
  shape: bbox 4.128 x 4.032 x 2e-07 mm, 0 faces, 0 solids (baked)
FEATURE [Part::Feature] path52377_09_3_5_7_6_0_0_2_2
  Placement = pos=(40.6315,-49.1329,0) rot=(0,0,1;0rad)
  shape: bbox 2.028 x 2.027 x 2e-07 mm, 0 faces, 0 solids (baked)
FEATURE [Part::Feature] path52401_71_2_5_9_2_7_5_4_9
  Placement = pos=(41.1315,-52.9329,0) rot=(0,0,1;0rad)
  shape: bbox 2.386 x 2.384 x 2e-07 mm, 0 faces, 0 solids (baked)
FEATURE [Part::Feature] path52401_7_8_1_1_7_3_8_4_4_6
  Placement = pos=(46.1315,-55.0329,0) rot=(0,0,1;0rad)
  shape: bbox 2.386 x 2.384 x 2e-07 mm, 0 faces, 0 solids (baked)
FEATURE [Part::Feature] path52377_0_5_0_1_9_1_0_6_9_1
  Placement = pos=(51.6315,-49.1329,0) rot=(0,0,1;0rad)
  shape: bbox 2.028 x 2.027 x 2e-07 mm, 0 faces, 0 solids (baked)
FEATURE [Part::Feature] path52456_0_5_2_2_2_9_9_3_1
  Placement = pos=(46.1315,-49.1329,0) rot=(0,0,1;0rad)
  shape: bbox 4.091 x 4.089 x 2e-07 mm, 0 faces, 0 solids (baked)
FEATURE [Part::Feature] path52377_09_3_5_7_6_6_7_9_0
  Placement = pos=(40.6315,-49.1329,0) rot=(0,0,1;0rad)
  shape: bbox 2 x 2.046 x 2e-07 mm, 0 faces, 0 solids (baked)
FEATURE [Part::Feature] path52401_71_2_5_9_2_1_4_5_2
  Placement = pos=(41.1315,-52.9329,0) rot=(0,0,1;0rad)
  shape: bbox 2.353 x 2.407 x 2e-07 mm, 0 faces, 0 solids (baked)
FEATURE [Part::Feature] path52401_7_8_1_1_7_3_1_9_1_9
  Placement = pos=(46.1315,-55.0329,0) rot=(0,0,1;0rad)
  shape: bbox 2.353 x 2.407 x 2e-07 mm, 0 faces, 0 solids (baked)
FEATURE [Part::Feature] path52377_0_5_0_1_9_1_3_9_3_6
  Placement = pos=(51.6315,-49.1329,0) rot=(0,0,1;0rad)
  shape: bbox 2 x 2.046 x 2e-07 mm, 0 faces, 0 solids (baked)
FEATURE [Part::Feature] path52456_0_5_2_2_2_5_8_5_5
  Placement = pos=(46.1315,-49.1329,0) rot=(0,0,1;0rad)
  shape: bbox 4.036 x 4.128 x 2e-07 mm, 0 faces, 0 solids (baked)
FEATURE [Part::Feature] path52377_09_3_5_7_6_4_7_2_2
  Placement = pos=(40.6315,-49.1329,0) rot=(0,0,1;0rad)
  shape: bbox 2.027 x 2.028 x 2e-07 mm, 0 faces, 0 solids (baked)
FEATURE [Part::Feature] path52401_71_2_5_9_2_8_0_6_1
  Placement = pos=(41.1315,-52.9329,0) rot=(0,0,1;0rad)
  shape: bbox 2.385 x 2.386 x 2e-07 mm, 0 faces, 0 solids (baked)
FEATURE [Part::Feature] path52401_7_8_1_1_7_3_6_7_6_3
  Placement = pos=(46.1315,-55.0329,0) rot=(0,0,1;0rad)
  shape: bbox 2.385 x 2.386 x 2e-07 mm, 0 faces, 0 solids (baked)
FEATURE [Part::Feature] path52377_0_5_0_1_9_1_4_7_5_3
  Placement = pos=(51.6315,-49.1329,0) rot=(0,0,1;0rad)
  shape: bbox 2.027 x 2.028 x 2e-07 mm, 0 faces, 0 solids (baked)
FEATURE [Part::Feature] path52456_0_5_2_2_2_7_4_6_3
  Placement = pos=(46.1315,-49.1329,0) rot=(0,0,1;0rad)
  shape: bbox 4.09 x 4.092 x 2e-07 mm, 0 faces, 0 solids (baked)
FEATURE [Part::Feature] path61609_4_5_7_9_4_80_0_8_2_8_3_3
  shape: bbox 15.78 x 7.528 x 2e-07 mm, 0 faces, 0 solids (baked)
FEATURE [Part::Feature] path61609_4_5_7_9_4_80_0_8_2_8_3_6_9
  shape: bbox 15.05 x 8.449 x 2e-07 mm, 0 faces, 0 solids (baked)
FEATURE [Part::Feature] path61609_4_5_7_9_4_80_0_8_2_8_3_69_9
  shape: bbox 14.53 x 10.59 x 2e-07 mm, 0 faces, 0 solids (baked)
FEATURE [Part::Feature] path61609_4_5_7_9_4_80_0_8_2_8_3_7_7
  shape: bbox 13.03 x 13.29 x 2e-07 mm, 0 faces, 0 solids (baked)
FEATURE [Part::Extrusion] Extrude012
  Base = -> path61609_4_5_7_9_4_80_0_5
  Dir = (0,0,1)
  DirMode = 0
  FaceMakerClass = Part::FaceMakerBullseye
  LengthFwd = 2
  LengthRev = 0
  Solid = true
  Symmetric = false
FEATURE [Part::Extrusion] Extrude013
  Base = -> path61609_4_5_7_9_4_80_0_3_2
  Dir = (0,0,1)
  DirMode = 0
  FaceMakerClass = Part::FaceMakerBullseye
  LengthFwd = 2
  LengthRev = 0
  Solid = true
  Symmetric = false
FEATURE [Part::Extrusion] Extrude014
  Base = -> path52377_09_3_1_8_87
  Dir = (0,0,1)
  DirMode = 0
  FaceMakerClass = Part::FaceMakerBullseye
  LengthFwd = 2
  LengthRev = 0
  Solid = true
  Symmetric = false
FEATURE [Part::Extrusion] Extrude015
  Base = -> path52401_71_2_4_9_8
  Dir = (0,0,1)
  DirMode = 0
  FaceMakerClass = Part::FaceMakerBullseye
  LengthFwd = 2
  LengthRev = 0
  Solid = true
  Symmetric = false
FEATURE [Part::Extrusion] Extrude016
  Base = -> path52401_7_8_1_8_2_30
  Dir = (0,0,1)
  DirMode = 0
  FaceMakerClass = Part::FaceMakerBullseye
  LengthFwd = 2
  LengthRev = 0
  Solid = true
  Symmetric = false
FEATURE [Part::Extrusion] Extrude017
  Base = -> path52377_0_5_0_4_2_3
  Dir = (0,0,1)
  DirMode = 0
  FaceMakerClass = Part::FaceMakerBullseye
  LengthFwd = 2
  LengthRev = 0
  Solid = true
  Symmetric = false
FEATURE [Part::Extrusion] Extrude018
  Base = -> path52456_0_5_5_7_86
  Dir = (0,0,1)
  DirMode = 0
  FaceMakerClass = Part::FaceMakerBullseye
  LengthFwd = 2
  LengthRev = 0
  Solid = true
  Symmetric = false
FEATURE [Part::Extrusion] Extrude019
  Base = -> path52377_09_3_1_8_8_2
  Dir = (0,0,1)
  DirMode = 0
  FaceMakerClass = Part::FaceMakerBullseye
  LengthFwd = 2
  LengthRev = 0
  Solid = true
  Symmetric = false
FEATURE [Part::Extrusion] Extrude020
  Base = -> path52401_71_2_4_9_4_5
  Dir = (0,0,1)
  DirMode = 0
  FaceMakerClass = Part::FaceMakerBullseye
  LengthFwd = 2
  LengthRev = 0
  Solid = true
  Symmetric = false
FEATURE [Part::Extrusion] Extrude021
  Base = -> path52401_7_8_1_8_2_3_11
  Dir = (0,0,1)
  DirMode = 0
  FaceMakerClass = Part::FaceMakerBullseye
  LengthFwd = 2
  LengthRev = 0
  Solid = true
  Symmetric = false
FEATURE [Part::Extrusion] Extrude022
  Base = -> path52377_0_5_0_4_2_4_5
  Dir = (0,0,1)
  DirMode = 0
  FaceMakerClass = Part::FaceMakerBullseye
  LengthFwd = 2
  LengthRev = 0
  Solid = true
  Symmetric = false
FEATURE [Part::Extrusion] Extrude023
  Base = -> path52456_0_5_5_7_7_0
  Dir = (0,0,1)
  DirMode = 0
  FaceMakerClass = Part::FaceMakerBullseye
  LengthFwd = 2
  LengthRev = 0
  Solid = true
  Symmetric = false
FEATURE [Part::Extrusion] Extrude024
  Base = -> path52377_09_3_1_8_2_3
  Dir = (0,0,1)
  DirMode = 0
  FaceMakerClass = Part::FaceMakerBullseye
  LengthFwd = 2
  LengthRev = 0
  Solid = true
  Symmetric = false
FEATURE [Part::Extrusion] Extrude025
  Base = -> path52401_71_2_4_9_2_39
  Dir = (0,0,1)
  DirMode = 0
  FaceMakerClass = Part::FaceMakerBullseye
  LengthFwd = 2
  LengthRev = 0
  Solid = true
  Symmetric = false
FEATURE [Part::Extrusion] Extrude026
  Base = -> path52401_7_8_1_8_2_31_2
  Dir = (0,0,1)
  DirMode = 0
  FaceMakerClass = Part::FaceMakerBullseye
  LengthFwd = 2
  LengthRev = 0
  Solid = true
  Symmetric = false
FEATURE [Part::Extrusion] Extrude027
  Base = -> path52377_0_5_0_4_2_41_1
  Dir = (0,0,1)
  DirMode = 0
  FaceMakerClass = Part::FaceMakerBullseye
  LengthFwd = 2
  LengthRev = 0
  Solid = true
  Symmetric = false
FEATURE [Part::Extrusion] Extrude028
  Base = -> path52456_0_5_5_7_4_2
  Dir = (0,0,1)
  DirMode = 0
  FaceMakerClass = Part::FaceMakerBullseye
  LengthFwd = 2
  LengthRev = 0
  Solid = true
  Symmetric = false
FEATURE [Part::Extrusion] Extrude029
  Base = -> path52377_09_3_1_8_2_4_7
  Dir = (0,0,1)
  DirMode = 0
  FaceMakerClass = Part::FaceMakerBullseye
  LengthFwd = 2
  LengthRev = 0
  Solid = true
  Symmetric = false
FEATURE [Part::Extrusion] Extrude030
  Base = -> path52401_71_2_4_9_2_9_8
  Dir = (0,0,1)
  DirMode = 0
  FaceMakerClass = Part::FaceMakerBullseye
  LengthFwd = 2
  LengthRev = 0
  Solid = true
  Symmetric = false
FEATURE [Part::Extrusion] Extrude031
  Base = -> path52401_7_8_1_8_2_31_5_4
  Dir = (0,0,1)
  DirMode = 0
  FaceMakerClass = Part::FaceMakerBullseye
  LengthFwd = 2
  LengthRev = 0
  Solid = true
  Symmetric = false
FEATURE [Part::Extrusion] Extrude032
  Base = -> path52377_0_5_0_4_2_41_0_0
  Dir = (0,0,1)
  DirMode = 0
  FaceMakerClass = Part::FaceMakerBullseye
  LengthFwd = 2
  LengthRev = 0
  Solid = true
  Symmetric = false
FEATURE [Part::Extrusion] Extrude033
  Base = -> path52456_0_5_5_7_4_4_1
  Dir = (0,0,1)
  DirMode = 0
  FaceMakerClass = Part::FaceMakerBullseye
  LengthFwd = 2
  LengthRev = 0
  Solid = true
  Symmetric = false
FEATURE [Part::Extrusion] Extrude034
  Base = -> path52377_09_3_1_8_8_0_3
  Dir = (0,0,1)
  DirMode = 0
  FaceMakerClass = Part::FaceMakerBullseye
  LengthFwd = 2
  LengthRev = 0
  Solid = true
  Symmetric = false
FEATURE [Part::Extrusion] Extrude035
  Base = -> path52401_71_2_4_9_4_2_0
  Dir = (0,0,1)
  DirMode = 0
  FaceMakerClass = Part::FaceMakerBullseye
  LengthFwd = 2
  LengthRev = 0
  Solid = true
  Symmetric = false
FEATURE [Part::Extrusion] Extrude036
  Base = -> path52401_7_8_1_8_2_3_5_0
  Dir = (0,0,1)
  DirMode = 0
  FaceMakerClass = Part::FaceMakerBullseye
  LengthFwd = 2
  LengthRev = 0
  Solid = true
  Symmetric = false
FEATURE [Part::Extrusion] Extrude037
  Base = -> path52377_0_5_0_4_2_4_4_3
  Dir = (0,0,1)
  DirMode = 0
  FaceMakerClass = Part::FaceMakerBullseye
  LengthFwd = 2
  LengthRev = 0
  Solid = true
  Symmetric = false
FEATURE [Part::Extrusion] Extrude038
  Base = -> path52456_0_5_5_7_7_7_7
  Dir = (0,0,1)
  DirMode = 0
  FaceMakerClass = Part::FaceMakerBullseye
  LengthFwd = 2
  LengthRev = 0
  Solid = true
  Symmetric = false
FEATURE [Part::Extrusion] Extrude039
  Base = -> path52377_09_3_1_8_2_9_7
  Dir = (0,0,1)
  DirMode = 0
  FaceMakerClass = Part::FaceMakerBullseye
  LengthFwd = 2
  LengthRev = 0
  Solid = true
  Symmetric = false
FEATURE [Part::Extrusion] Extrude040
  Base = -> path52401_71_2_4_9_2_6_0
  Dir = (0,0,1)
  DirMode = 0
  FaceMakerClass = Part::FaceMakerBullseye
  LengthFwd = 2
  LengthRev = 0
  Solid = true
  Symmetric = false
FEATURE [Part::Extrusion] Extrude041
  Base = -> path52401_7_8_1_8_2_31_56_74
  Dir = (0,0,1)
  DirMode = 0
  FaceMakerClass = Part::FaceMakerBullseye
  LengthFwd = 2
  LengthRev = 0
  Solid = true
  Symmetric = false
FEATURE [Part::Extrusion] Extrude042
  Base = -> path52377_0_5_0_4_2_41_4_91
  Dir = (0,0,1)
  DirMode = 0
  FaceMakerClass = Part::FaceMakerBullseye
  LengthFwd = 2
  LengthRev = 0
  Solid = true
  Symmetric = false
FEATURE [Part::Extrusion] Extrude043
  Base = -> path52456_0_5_5_7_4_40_0
  Dir = (0,0,1)
  DirMode = 0
  FaceMakerClass = Part::FaceMakerBullseye
  LengthFwd = 2
  LengthRev = 0
  Solid = true
  Symmetric = false
FEATURE [Part::Extrusion] Extrude044
  Base = -> path52377_09_3_1_8_2_4_0_1
  Dir = (0,0,1)
  DirMode = 0
  FaceMakerClass = Part::FaceMakerBullseye
  LengthFwd = 2
  LengthRev = 0
  Solid = true
  Symmetric = false
FEATURE [Part::Extrusion] Extrude045
  Base = -> path52401_71_2_4_9_2_9_9_55
  Dir = (0,0,1)
  DirMode = 0
  FaceMakerClass = Part::FaceMakerBullseye
  LengthFwd = 2
  LengthRev = 0
  Solid = true
  Symmetric = false
FEATURE [Part::Extrusion] Extrude046
  Base = -> path52401_7_8_1_8_2_31_5_9_4
  Dir = (0,0,1)
  DirMode = 0
  FaceMakerClass = Part::FaceMakerBullseye
  LengthFwd = 2
  LengthRev = 0
  Solid = true
  Symmetric = false
FEATURE [Part::Extrusion] Extrude047
  Base = -> path52377_0_5_0_4_2_41_0_4_8
  Dir = (0,0,1)
  DirMode = 0
  FaceMakerClass = Part::FaceMakerBullseye
  LengthFwd = 2
  LengthRev = 0
  Solid = true
  Symmetric = false
FEATURE [Part::Extrusion] Extrude048
  Base = -> path52456_0_5_5_7_4_4_8_02
  Dir = (0,0,1)
  DirMode = 0
  FaceMakerClass = Part::FaceMakerBullseye
  LengthFwd = 2
  LengthRev = 0
  Solid = true
  Symmetric = false
FEATURE [Part::Extrusion] Extrude049
  Base = -> path52377_09_3_1_8_8_0_4_7
  Dir = (0,0,1)
  DirMode = 0
  FaceMakerClass = Part::FaceMakerBullseye
  LengthFwd = 2
  LengthRev = 0
  Solid = true
  Symmetric = false
FEATURE [Part::Extrusion] Extrude050
  Base = -> path52401_71_2_4_9_4_2_2_1
  Dir = (0,0,1)
  DirMode = 0
  FaceMakerClass = Part::FaceMakerBullseye
  LengthFwd = 2
  LengthRev = 0
  Solid = true
  Symmetric = false
FEATURE [Part::Extrusion] Extrude051
  Base = -> path52401_7_8_1_8_2_3_5_3_8
  Dir = (0,0,1)
  DirMode = 0
  FaceMakerClass = Part::FaceMakerBullseye
  LengthFwd = 2
  LengthRev = 0
  Solid = true
  Symmetric = false
FEATURE [Part::Extrusion] Extrude052
  Base = -> path52377_0_5_0_4_2_4_4_8_3
  Dir = (0,0,1)
  DirMode = 0
  FaceMakerClass = Part::FaceMakerBullseye
  LengthFwd = 2
  LengthRev = 0
  Solid = true
  Symmetric = false
FEATURE [Part::Extrusion] Extrude053
  Base = -> path52456_0_5_5_7_7_7_1_3
  Dir = (0,0,1)
  DirMode = 0
  FaceMakerClass = Part::FaceMakerBullseye
  LengthFwd = 2
  LengthRev = 0
  Solid = true
  Symmetric = false
FEATURE [Part::Extrusion] Extrude054
  Base = -> path52377_09_3_1_8_2_9_5_3
  Dir = (0,0,1)
  DirMode = 0
  FaceMakerClass = Part::FaceMakerBullseye
  LengthFwd = 2
  LengthRev = 0
  Solid = true
  Symmetric = false
FEATURE [Part::Extrusion] Extrude055
  Base = -> path52401_71_2_4_9_2_6_3_64
  Dir = (0,0,1)
  DirMode = 0
  FaceMakerClass = Part::FaceMakerBullseye
  LengthFwd = 2
  LengthRev = 0
  Solid = true
  Symmetric = false
FEATURE [Part::Extrusion] Extrude056
  Base = -> path52401_7_8_1_8_2_31_56_1_9
  Dir = (0,0,1)
  DirMode = 0
  FaceMakerClass = Part::FaceMakerBullseye
  LengthFwd = 2
  LengthRev = 0
  Solid = true
  Symmetric = false
FEATURE [Part::Extrusion] Extrude057
  Base = -> path52377_0_5_0_4_2_41_4_8_1
  Dir = (0,0,1)
  DirMode = 0
  FaceMakerClass = Part::FaceMakerBullseye
  LengthFwd = 2
  LengthRev = 0
  Solid = true
  Symmetric = false
FEATURE [Part::Extrusion] Extrude058
  Base = -> path52456_0_5_5_7_4_40_5_0
  Dir = (0,0,1)
  DirMode = 0
  FaceMakerClass = Part::FaceMakerBullseye
  LengthFwd = 2
  LengthRev = 0
  Solid = true
  Symmetric = false
FEATURE [Part::Extrusion] Extrude059
  Base = -> path52377_09_3_1_8_2_4_0_5_8
  Dir = (0,0,1)
  DirMode = 0
  FaceMakerClass = Part::FaceMakerBullseye
  LengthFwd = 2
  LengthRev = 0
  Solid = true
  Symmetric = false
FEATURE [Part::Extrusion] Extrude060
  Base = -> path52401_71_2_4_9_2_9_9_5_64
  Dir = (0,0,1)
  DirMode = 0
  FaceMakerClass = Part::FaceMakerBullseye
  LengthFwd = 2
  LengthRev = 0
  Solid = true
  Symmetric = false
FEATURE [Part::Extrusion] Extrude061
  Base = -> path52401_7_8_1_8_2_31_5_9_9_9
  Dir = (0,0,1)
  DirMode = 0
  FaceMakerClass = Part::FaceMakerBullseye
  LengthFwd = 2
  LengthRev = 0
  Solid = true
  Symmetric = false
FEATURE [Part::Extrusion] Extrude062
  Base = -> path52377_0_5_0_4_2_41_0_4_1_4
  Dir = (0,0,1)
  DirMode = 0
  FaceMakerClass = Part::FaceMakerBullseye
  LengthFwd = 2
  LengthRev = 0
  Solid = true
  Symmetric = false
FEATURE [Part::Extrusion] Extrude063
  Base = -> path52456_0_5_5_7_4_4_8_5_4
  Dir = (0,0,1)
  DirMode = 0
  FaceMakerClass = Part::FaceMakerBullseye
  LengthFwd = 2
  LengthRev = 0
  Solid = true
  Symmetric = false
FEATURE [Part::Extrusion] Extrude064
  Base = -> path52377_09_3_1_8_8_0_4_5_6
  Dir = (0,0,1)
  DirMode = 0
  FaceMakerClass = Part::FaceMakerBullseye
  LengthFwd = 2
  LengthRev = 0
  Solid = true
  Symmetric = false
FEATURE [Part::Extrusion] Extrude065
  Base = -> path52401_71_2_4_9_4_2_2_8_5
  Dir = (0,0,1)
  DirMode = 0
  FaceMakerClass = Part::FaceMakerBullseye
  LengthFwd = 2
  LengthRev = 0
  Solid = true
  Symmetric = false
FEATURE [Part::Extrusion] Extrude066
  Base = -> path52401_7_8_1_8_2_3_5_3_4_2
  Dir = (0,0,1)
  DirMode = 0
  FaceMakerClass = Part::FaceMakerBullseye
  LengthFwd = 2
  LengthRev = 0
  Solid = true
  Symmetric = false
FEATURE [Part::Extrusion] Extrude067
  Base = -> path52377_0_5_0_4_2_4_4_8_9_1
  Dir = (0,0,1)
  DirMode = 0
  FaceMakerClass = Part::FaceMakerBullseye
  LengthFwd = 2
  LengthRev = 0
  Solid = true
  Symmetric = false
FEATURE [Part::Extrusion] Extrude068
  Base = -> path52456_0_5_5_7_7_7_1_7_8
  Dir = (0,0,1)
  DirMode = 0
  FaceMakerClass = Part::FaceMakerBullseye
  LengthFwd = 2
  LengthRev = 0
  Solid = true
  Symmetric = false
FEATURE [Part::Extrusion] Extrude069
  Base = -> path52377_09_3_1_8_2_9_5_4_8
  Dir = (0,0,1)
  DirMode = 0
  FaceMakerClass = Part::FaceMakerBullseye
  LengthFwd = 2
  LengthRev = 0
  Solid = true
  Symmetric = false
FEATURE [Part::Extrusion] Extrude070
  Base = -> path52401_71_2_4_9_2_6_3_6_9
  Dir = (0,0,1)
  DirMode = 0
  FaceMakerClass = Part::FaceMakerBullseye
  LengthFwd = 2
  LengthRev = 0
  Solid = true
  Symmetric = false
FEATURE [Part::Extrusion] Extrude071
  Base = -> path52401_7_8_1_8_2_31_56_1_3_7
  Dir = (0,0,1)
  DirMode = 0
  FaceMakerClass = Part::FaceMakerBullseye
  LengthFwd = 2
  LengthRev = 0
  Solid = true
  Symmetric = false
FEATURE [Part::Extrusion] Extrude072
  Base = -> path52377_0_5_0_4_2_41_4_8_8_6
  Dir = (0,0,1)
  DirMode = 0
  FaceMakerClass = Part::FaceMakerBullseye
  LengthFwd = 2
  LengthRev = 0
  Solid = true
  Symmetric = false
FEATURE [Part::Extrusion] Extrude073
  Base = -> path52456_0_5_5_7_4_40_5_1_45
  Dir = (0,0,1)
  DirMode = 0
  FaceMakerClass = Part::FaceMakerBullseye
  LengthFwd = 2
  LengthRev = 0
  Solid = true
  Symmetric = false
FEATURE [Part::Extrusion] Extrude074
  Base = -> path52377_09_3_1_8_2_4_0_5_0_4
  Dir = (0,0,1)
  DirMode = 0
  FaceMakerClass = Part::FaceMakerBullseye
  LengthFwd = 2
  LengthRev = 0
  Solid = true
  Symmetric = false
FEATURE [Part::Extrusion] Extrude075
  Base = -> path52401_71_2_4_9_2_9_9_5_6_8
  Dir = (0,0,1)
  DirMode = 0
  FaceMakerClass = Part::FaceMakerBullseye
  LengthFwd = 2
  LengthRev = 0
  Solid = true
  Symmetric = false
FEATURE [Part::Extrusion] Extrude076
  Base = -> path52401_7_8_1_8_2_31_5_9_9_0_0
  Dir = (0,0,1)
  DirMode = 0
  FaceMakerClass = Part::FaceMakerBullseye
  LengthFwd = 2
  LengthRev = 0
  Solid = true
  Symmetric = false
FEATURE [Part::Extrusion] Extrude077
  Base = -> path52377_0_5_0_4_2_41_0_4_1_8_44
  Dir = (0,0,1)
  DirMode = 0
  FaceMakerClass = Part::FaceMakerBullseye
  LengthFwd = 2
  LengthRev = 0
  Solid = true
  Symmetric = false
FEATURE [Part::Extrusion] Extrude078
  Base = -> path52456_0_5_5_7_4_4_8_5_8_8
  Dir = (0,0,1)
  DirMode = 0
  FaceMakerClass = Part::FaceMakerBullseye
  LengthFwd = 2
  LengthRev = 0
  Solid = true
  Symmetric = false
FEATURE [Part::Extrusion] Extrude079
  Base = -> path52377_09_3_1_8_8_0_4_5_8_91
  Dir = (0,0,1)
  DirMode = 0
  FaceMakerClass = Part::FaceMakerBullseye
  LengthFwd = 2
  LengthRev = 0
  Solid = true
  Symmetric = false
FEATURE [Part::Extrusion] Extrude080
  Base = -> path52401_71_2_4_9_4_2_2_8_7_5
  Dir = (0,0,1)
  DirMode = 0
  FaceMakerClass = Part::FaceMakerBullseye
  LengthFwd = 2
  LengthRev = 0
  Solid = true
  Symmetric = false
FEATURE [Part::Extrusion] Extrude081
  Base = -> path52401_7_8_1_8_2_3_5_3_4_4_44
  Dir = (0,0,1)
  DirMode = 0
  FaceMakerClass = Part::FaceMakerBullseye
  LengthFwd = 2
  LengthRev = 0
  Solid = true
  Symmetric = false
FEATURE [Part::Extrusion] Extrude082
  Base = -> path52377_0_5_0_4_2_4_4_8_9_2_9
  Dir = (0,0,1)
  DirMode = 0
  FaceMakerClass = Part::FaceMakerBullseye
  LengthFwd = 2
  LengthRev = 0
  Solid = true
  Symmetric = false
FEATURE [Part::Extrusion] Extrude083
  Base = -> path52456_0_5_5_7_7_7_1_7_0_2
  Dir = (0,0,1)
  DirMode = 0
  FaceMakerClass = Part::FaceMakerBullseye
  LengthFwd = 2
  LengthRev = 0
  Solid = true
  Symmetric = false
FEATURE [Part::Extrusion] Extrude084
  Base = -> path52377_09_3_1_8_2_9_5_4_9_5
  Dir = (0,0,1)
  DirMode = 0
  FaceMakerClass = Part::FaceMakerBullseye
  LengthFwd = 2
  LengthRev = 0
  Solid = true
  Symmetric = false
FEATURE [Part::Extrusion] Extrude085
  Base = -> path52401_71_2_4_9_2_6_3_6_8_5
  Dir = (0,0,1)
  DirMode = 0
  FaceMakerClass = Part::FaceMakerBullseye
  LengthFwd = 2
  LengthRev = 0
  Solid = true
  Symmetric = false
FEATURE [Part::Extrusion] Extrude086
  Base = -> path52401_7_8_1_8_2_31_56_1_3_0_2
  Dir = (0,0,1)
  DirMode = 0
  FaceMakerClass = Part::FaceMakerBullseye
  LengthFwd = 2
  LengthRev = 0
  Solid = true
  Symmetric = false
FEATURE [Part::Extrusion] Extrude087
  Base = -> path52377_0_5_0_4_2_41_4_8_8_0_5
  Dir = (0,0,1)
  DirMode = 0
  FaceMakerClass = Part::FaceMakerBullseye
  LengthFwd = 2
  LengthRev = 0
  Solid = true
  Symmetric = false
FEATURE [Part::Extrusion] Extrude088
  Base = -> path52456_0_5_5_7_4_40_5_1_5_56
  Dir = (0,0,1)
  DirMode = 0
  FaceMakerClass = Part::FaceMakerBullseye
  LengthFwd = 2
  LengthRev = 0
  Solid = true
  Symmetric = false
FEATURE [Part::Extrusion] Extrude089
  Base = -> path52377_09_3_1_8_2_4_0_5_0_2_7
  Dir = (0,0,1)
  DirMode = 0
  FaceMakerClass = Part::FaceMakerBullseye
  LengthFwd = 2
  LengthRev = 0
  Solid = true
  Symmetric = false
FEATURE [Part::Extrusion] Extrude090
  Base = -> path52401_71_2_4_9_2_9_9_5_6_2_6
  Dir = (0,0,1)
  DirMode = 0
  FaceMakerClass = Part::FaceMakerBullseye
  LengthFwd = 2
  LengthRev = 0
  Solid = true
  Symmetric = false
FEATURE [Part::Extrusion] Extrude091
  Base = -> path52401_7_8_1_8_2_31_5_9_9_0_7_2
  Dir = (0,0,1)
  DirMode = 0
  FaceMakerClass = Part::FaceMakerBullseye
  LengthFwd = 2
  LengthRev = 0
  Solid = true
  Symmetric = false
FEATURE [Part::Extrusion] Extrude092
  Base = -> path52377_0_5_0_4_2_41_0_4_1_8_4_4
  Dir = (0,0,1)
  DirMode = 0
  FaceMakerClass = Part::FaceMakerBullseye
  LengthFwd = 2
  LengthRev = 0
  Solid = true
  Symmetric = false
FEATURE [Part::Extrusion] Extrude093
  Base = -> path52456_0_5_5_7_4_4_8_5_8_0_3
  Dir = (0,0,1)
  DirMode = 0
  FaceMakerClass = Part::FaceMakerBullseye
  LengthFwd = 2
  LengthRev = 0
  Solid = true
  Symmetric = false
FEATURE [Part::Extrusion] Extrude094
  Base = -> path52377_09_3_1_8_8_0_4_5_8_9_1
  Dir = (0,0,1)
  DirMode = 0
  FaceMakerClass = Part::FaceMakerBullseye
  LengthFwd = 2
  LengthRev = 0
  Solid = true
  Symmetric = false
FEATURE [Part::Extrusion] Extrude095
  Base = -> path52401_71_2_4_9_4_2_2_8_7_6_2
  Dir = (0,0,1)
  DirMode = 0
  FaceMakerClass = Part::FaceMakerBullseye
  LengthFwd = 2
  LengthRev = 0
  Solid = true
  Symmetric = false
FEATURE [Part::Extrusion] Extrude096
  Base = -> path52401_7_8_1_8_2_3_5_3_4_4_8_8
  Dir = (0,0,1)
  DirMode = 0
  FaceMakerClass = Part::FaceMakerBullseye
  LengthFwd = 2
  LengthRev = 0
  Solid = true
  Symmetric = false
FEATURE [Part::Extrusion] Extrude097
  Base = -> path52377_0_5_0_4_2_4_4_8_9_2_0_5
  Dir = (0,0,1)
  DirMode = 0
  FaceMakerClass = Part::FaceMakerBullseye
  LengthFwd = 2
  LengthRev = 0
  Solid = true
  Symmetric = false
FEATURE [Part::Extrusion] Extrude098
  Base = -> path52456_0_5_5_7_7_7_1_7_0_0_6
  Dir = (0,0,1)
  DirMode = 0
  FaceMakerClass = Part::FaceMakerBullseye
  LengthFwd = 2
  LengthRev = 0
  Solid = true
  Symmetric = false
FEATURE [Part::Extrusion] Extrude099
  Base = -> circle37307_9_0_7_1
  Dir = (0,0,1)
  DirMode = 0
  FaceMakerClass = Part::FaceMakerBullseye
  LengthFwd = 2
  LengthRev = 0
  Solid = true
  Symmetric = false
FEATURE [Part::Extrusion] Extrude100
  Base = -> circle37313_0_5_2_6
  Dir = (0,0,1)
  DirMode = 0
  FaceMakerClass = Part::FaceMakerBullseye
  LengthFwd = 2
  LengthRev = 0
  Solid = true
  Symmetric = false
FEATURE [Part::Extrusion] Extrude101
  Base = -> path8_2
  Dir = (0,0,1)
  DirMode = 0
  FaceMakerClass = Part::FaceMakerBullseye
  LengthFwd = 2
  LengthRev = 0
  Solid = true
  Symmetric = false
FEATURE [Part::Extrusion] Extrude102
  Base = -> path4_1
  Dir = (0,0,1)
  DirMode = 0
  FaceMakerClass = Part::FaceMakerBullseye
  LengthFwd = 2
  LengthRev = 0
  Solid = true
  Symmetric = false
FEATURE [Part::Extrusion] Extrude103
  Base = -> path6_5
  Dir = (0,0,1)
  DirMode = 0
  FaceMakerClass = Part::FaceMakerBullseye
  LengthFwd = 2
  LengthRev = 0
  Solid = true
  Symmetric = false
FEATURE [Part::Extrusion] Extrude104
  Base = -> path2_5
  Dir = (0,0,1)
  DirMode = 0
  FaceMakerClass = Part::FaceMakerBullseye
  LengthFwd = 2
  LengthRev = 0
  Solid = true
  Symmetric = false
FEATURE [Part::Extrusion] Extrude105
  Base = -> path37931_6_3_3
  Dir = (0,0,1)
  DirMode = 0
  FaceMakerClass = Part::FaceMakerBullseye
  LengthFwd = 2
  LengthRev = 0
  Solid = true
  Symmetric = false
FEATURE [Part::Extrusion] Extrude106
  Base = -> path37937_8_1_8
  Dir = (0,0,1)
  DirMode = 0
  FaceMakerClass = Part::FaceMakerBullseye
  LengthFwd = 2
  LengthRev = 0
  Solid = true
  Symmetric = false
FEATURE [Part::Extrusion] Extrude107
  Base = -> rect117948_1_5_1_8
  Dir = (0,0,1)
  DirMode = 0
  FaceMakerClass = Part::FaceMakerBullseye
  LengthFwd = 2
  LengthRev = 0
  Solid = true
  Symmetric = false
FEATURE [Part::Extrusion] Extrude108
  Base = -> rect117948_2_0_8_5_8
  Dir = (0,0,1)
  DirMode = 0
  FaceMakerClass = Part::FaceMakerBullseye
  LengthFwd = 2
  LengthRev = 0
  Solid = true
  Symmetric = false
FEATURE [Part::Extrusion] Extrude109
  Base = -> path61609_4_5_7_9_4_80_0_8_78
  Dir = (0,0,1)
  DirMode = 0
  FaceMakerClass = Part::FaceMakerBullseye
  LengthFwd = 2
  LengthRev = 0
  Solid = true
  Symmetric = false
FEATURE [Part::Extrusion] Extrude110
  Base = -> path61609_4_5_7_9_4_80_0_3_8_68
  Dir = (0,0,1)
  DirMode = 0
  FaceMakerClass = Part::FaceMakerBullseye
  LengthFwd = 2
  LengthRev = 0
  Solid = true
  Symmetric = false
FEATURE [Part::Extrusion] Extrude111
  Base = -> path61609_4_5_7_9_4_80_0_3_8_6_79
  Dir = (0,0,1)
  DirMode = 0
  FaceMakerClass = Part::FaceMakerBullseye
  LengthFwd = 2
  LengthRev = 0
  Solid = true
  Symmetric = false
FEATURE [Part::Extrusion] Extrude112
  Base = -> path61609_4_5_7_9_4_80_0_8_3_5
  Dir = (0,0,1)
  DirMode = 0
  FaceMakerClass = Part::FaceMakerBullseye
  LengthFwd = 2
  LengthRev = 0
  Solid = true
  Symmetric = false
FEATURE [Part::Extrusion] Extrude113
  Base = -> path61609_4_5_7_9_4_80_0_3_8_9_3
  Dir = (0,0,1)
  DirMode = 0
  FaceMakerClass = Part::FaceMakerBullseye
  LengthFwd = 2
  LengthRev = 0
  Solid = true
  Symmetric = false
FEATURE [Part::Extrusion] Extrude114
  Base = -> path61609_4_5_7_9_4_80_0_3_8_6_1_2
  Dir = (0,0,1)
  DirMode = 0
  FaceMakerClass = Part::FaceMakerBullseye
  LengthFwd = 2
  LengthRev = 0
  Solid = true
  Symmetric = false
FEATURE [Part::Extrusion] Extrude115
  Base = -> path61609_4_5_7_9_4_80_0_8_7_0
  Dir = (0,0,1)
  DirMode = 0
  FaceMakerClass = Part::FaceMakerBullseye
  LengthFwd = 2
  LengthRev = 0
  Solid = true
  Symmetric = false
FEATURE [Part::Extrusion] Extrude116
  Base = -> path61609_4_5_7_9_4_80_0_3_8_91_1
  Dir = (0,0,1)
  DirMode = 0
  FaceMakerClass = Part::FaceMakerBullseye
  LengthFwd = 2
  LengthRev = 0
  Solid = true
  Symmetric = false
FEATURE [Part::Extrusion] Extrude117
  Base = -> path61609_4_5_7_9_4_80_0_3_8_6_3_6
  Dir = (0,0,1)
  DirMode = 0
  FaceMakerClass = Part::FaceMakerBullseye
  LengthFwd = 2
  LengthRev = 0
  Solid = true
  Symmetric = false
FEATURE [Part::Extrusion] Extrude118
  Base = -> path61609_4_5_7_9_4_80_0_8_8_6
  Dir = (0,0,1)
  DirMode = 0
  FaceMakerClass = Part::FaceMakerBullseye
  LengthFwd = 2
  LengthRev = 0
  Solid = true
  Symmetric = false
FEATURE [Part::Extrusion] Extrude119
  Base = -> path61609_4_5_7_9_4_80_0_3_8_0_9
  Dir = (0,0,1)
  DirMode = 0
  FaceMakerClass = Part::FaceMakerBullseye
  LengthFwd = 2
  LengthRev = 0
  Solid = true
  Symmetric = false
FEATURE [Part::Extrusion] Extrude120
  Base = -> path61609_4_5_7_9_4_80_0_3_8_6_7_8
  Dir = (0,0,1)
  DirMode = 0
  FaceMakerClass = Part::FaceMakerBullseye
  LengthFwd = 2
  LengthRev = 0
  Solid = true
  Symmetric = false
FEATURE [Part::Extrusion] Extrude121
  Base = -> path61609_4_5_7_9_4_80_0_8_2_6
  Dir = (0,0,1)
  DirMode = 0
  FaceMakerClass = Part::FaceMakerBullseye
  LengthFwd = 2
  LengthRev = 0
  Solid = true
  Symmetric = false
FEATURE [Part::Extrusion] Extrude122
  Base = -> path61609_4_5_7_9_4_80_0_3_8_60_6
  Dir = (0,0,1)
  DirMode = 0
  FaceMakerClass = Part::FaceMakerBullseye
  LengthFwd = 2
  LengthRev = 0
  Solid = true
  Symmetric = false
FEATURE [Part::Extrusion] Extrude123
  Base = -> path61609_4_5_7_9_4_80_0_3_8_6_4_2
  Dir = (0,0,1)
  DirMode = 0
  FaceMakerClass = Part::FaceMakerBullseye
  LengthFwd = 2
  LengthRev = 0
  Solid = true
  Symmetric = false
FEATURE [Part::Extrusion] Extrude124
  Base = -> path52377_09_3_5_7_6_7_3_2
  Dir = (0,0,1)
  DirMode = 0
  FaceMakerClass = Part::FaceMakerBullseye
  LengthFwd = 2
  LengthRev = 0
  Solid = true
  Symmetric = false
FEATURE [Part::Extrusion] Extrude125
  Base = -> path52401_71_2_5_9_2_77_3_4
  Dir = (0,0,1)
  DirMode = 0
  FaceMakerClass = Part::FaceMakerBullseye
  LengthFwd = 2
  LengthRev = 0
  Solid = true
  Symmetric = false
FEATURE [Part::Extrusion] Extrude126
  Base = -> path52401_7_8_1_1_7_3_9_0_7
  Dir = (0,0,1)
  DirMode = 0
  FaceMakerClass = Part::FaceMakerBullseye
  LengthFwd = 2
  LengthRev = 0
  Solid = true
  Symmetric = false
FEATURE [Part::Extrusion] Extrude127
  Base = -> path52377_0_5_0_1_9_1_5_5_6
  Dir = (0,0,1)
  DirMode = 0
  FaceMakerClass = Part::FaceMakerBullseye
  LengthFwd = 2
  LengthRev = 0
  Solid = true
  Symmetric = false
FEATURE [Part::Extrusion] Extrude128
  Base = -> path52456_0_5_2_2_2_3_5_8
  Dir = (0,0,1)
  DirMode = 0
  FaceMakerClass = Part::FaceMakerBullseye
  LengthFwd = 2
  LengthRev = 0
  Solid = true
  Symmetric = false
FEATURE [Part::Extrusion] Extrude129
  Base = -> path52377_09_3_5_7_6_0_0_2_2
  Dir = (0,0,1)
  DirMode = 0
  FaceMakerClass = Part::FaceMakerBullseye
  LengthFwd = 2
  LengthRev = 0
  Solid = true
  Symmetric = false
FEATURE [Part::Extrusion] Extrude130
  Base = -> path52401_71_2_5_9_2_7_5_4_9
  Dir = (0,0,1)
  DirMode = 0
  FaceMakerClass = Part::FaceMakerBullseye
  LengthFwd = 2
  LengthRev = 0
  Solid = true
  Symmetric = false
FEATURE [Part::Extrusion] Extrude131
  Base = -> path52401_7_8_1_1_7_3_8_4_4_6
  Dir = (0,0,1)
  DirMode = 0
  FaceMakerClass = Part::FaceMakerBullseye
  LengthFwd = 2
  LengthRev = 0
  Solid = true
  Symmetric = false
FEATURE [Part::Extrusion] Extrude132
  Base = -> path52377_0_5_0_1_9_1_0_6_9_1
  Dir = (0,0,1)
  DirMode = 0
  FaceMakerClass = Part::FaceMakerBullseye
  LengthFwd = 2
  LengthRev = 0
  Solid = true
  Symmetric = false
FEATURE [Part::Extrusion] Extrude133
  Base = -> path52456_0_5_2_2_2_9_9_3_1
  Dir = (0,0,1)
  DirMode = 0
  FaceMakerClass = Part::FaceMakerBullseye
  LengthFwd = 2
  LengthRev = 0
  Solid = true
  Symmetric = false
FEATURE [Part::Extrusion] Extrude134
  Base = -> path52377_09_3_5_7_6_6_7_9_0
  Dir = (0,0,1)
  DirMode = 0
  FaceMakerClass = Part::FaceMakerBullseye
  LengthFwd = 2
  LengthRev = 0
  Solid = true
  Symmetric = false
FEATURE [Part::Extrusion] Extrude135
  Base = -> path52401_71_2_5_9_2_1_4_5_2
  Dir = (0,0,1)
  DirMode = 0
  FaceMakerClass = Part::FaceMakerBullseye
  LengthFwd = 2
  LengthRev = 0
  Solid = true
  Symmetric = false
FEATURE [Part::Extrusion] Extrude136
  Base = -> path52401_7_8_1_1_7_3_1_9_1_9
  Dir = (0,0,1)
  DirMode = 0
  FaceMakerClass = Part::FaceMakerBullseye
  LengthFwd = 2
  LengthRev = 0
  Solid = true
  Symmetric = false
FEATURE [Part::Extrusion] Extrude137
  Base = -> path52377_0_5_0_1_9_1_3_9_3_6
  Dir = (0,0,1)
  DirMode = 0
  FaceMakerClass = Part::FaceMakerBullseye
  LengthFwd = 2
  LengthRev = 0
  Solid = true
  Symmetric = false
FEATURE [Part::Extrusion] Extrude138
  Base = -> path52456_0_5_2_2_2_5_8_5_5
  Dir = (0,0,1)
  DirMode = 0
  FaceMakerClass = Part::FaceMakerBullseye
  LengthFwd = 2
  LengthRev = 0
  Solid = true
  Symmetric = false
FEATURE [Part::Extrusion] Extrude139
  Base = -> path52377_09_3_5_7_6_4_7_2_2
  Dir = (0,0,1)
  DirMode = 0
  FaceMakerClass = Part::FaceMakerBullseye
  LengthFwd = 2
  LengthRev = 0
  Solid = true
  Symmetric = false
FEATURE [Part::Extrusion] Extrude140
  Base = -> path52401_71_2_5_9_2_8_0_6_1
  Dir = (0,0,1)
  DirMode = 0
  FaceMakerClass = Part::FaceMakerBullseye
  LengthFwd = 2
  LengthRev = 0
  Solid = true
  Symmetric = false
FEATURE [Part::Extrusion] Extrude141
  Base = -> path52401_7_8_1_1_7_3_6_7_6_3
  Dir = (0,0,1)
  DirMode = 0
  FaceMakerClass = Part::FaceMakerBullseye
  LengthFwd = 2
  LengthRev = 0
  Solid = true
  Symmetric = false
FEATURE [Part::Extrusion] Extrude142
  Base = -> path52377_0_5_0_1_9_1_4_7_5_3
  Dir = (0,0,1)
  DirMode = 0
  FaceMakerClass = Part::FaceMakerBullseye
  LengthFwd = 2
  LengthRev = 0
  Solid = true
  Symmetric = false
FEATURE [Part::Extrusion] Extrude143
  Base = -> path52456_0_5_2_2_2_7_4_6_3
  Dir = (0,0,1)
  DirMode = 0
  FaceMakerClass = Part::FaceMakerBullseye
  LengthFwd = 2
  LengthRev = 0
  Solid = true
  Symmetric = false
FEATURE [Part::Extrusion] Extrude144
  Base = -> path61609_4_5_7_9_4_80_0_8_2_8_3_3
  Dir = (0,0,1)
  DirMode = 0
  FaceMakerClass = Part::FaceMakerBullseye
  LengthFwd = 2
  LengthRev = 0
  Solid = true
  Symmetric = false
FEATURE [Part::Extrusion] Extrude145
  Base = -> path61609_4_5_7_9_4_80_0_8_2_8_3_6_9
  Dir = (0,0,1)
  DirMode = 0
  FaceMakerClass = Part::FaceMakerBullseye
  LengthFwd = 2
  LengthRev = 0
  Solid = true
  Symmetric = false
FEATURE [Part::Extrusion] Extrude146
  Base = -> path61609_4_5_7_9_4_80_0_8_2_8_3_69_9
  Dir = (0,0,1)
  DirMode = 0
  FaceMakerClass = Part::FaceMakerBullseye
  LengthFwd = 2
  LengthRev = 0
  Solid = true
  Symmetric = false
FEATURE [Part::Extrusion] Extrude147
  Base = -> path61609_4_5_7_9_4_80_0_8_2_8_3_7_7
  Dir = (0,0,1)
  DirMode = 0
  FaceMakerClass = Part::FaceMakerBullseye
  LengthFwd = 2
  LengthRev = 0
  Solid = true
  Symmetric = false
FEATURE [Part::MultiFuse] Fusion001  label="wells_left"
  Placement = pos=(0,0,1) rot=(0,0,1;0rad)
  Shapes = -> [Extrude012,Extrude013,Extrude014,Extrude015,Extrude016,Extrude017,Extrude018,Extrude019,Extrude020,Extrude021,Extrude022,Extrude023,Extrude024,Extrude025,Extrude026,Extrude027,Extrude028,Extrude029,Extrude030,Extrude031,Extrude032,Extrude033,Extrude034,Extrude035,Extrude036,Extrude037,Extrude038,Extrude039,Extrude040,Extrude041,Extrude042,Extrude043,Extrude044,Extrude045,Extrude046,Extrude047,+100 more]
FEATURE [Part::FeaturePython] XOR  label="left"  # WARN: FeaturePython — macro-defined, semantics opaque (R4)
  Objects = -> [Extrude,Extrude001,Fusion,Fusion001]
  Tolerance = 0
FEATURE [Part::Feature] path44149_5_004
  shape: bbox 139.5 x 94.73 x 2e-07 mm, 0 faces, 0 solids (baked)
FEATURE [Part::Extrusion] Extrude149  label="inner_right"
  Base = -> path44149_5_004
  Dir = (0,0,1)
  DirMode = 0
  FaceMakerClass = Part::FaceMakerBullseye
  LengthFwd = 0.8
  LengthRev = 0
  Placement = pos=(0,0,3) rot=(0,0,1;0rad)
  Solid = true
  Symmetric = false
FEATURE [Part::Feature] path44149_5_005
  shape: bbox 145.5 x 102.4 x 2e-07 mm, 0 faces, 0 solids (baked)
FEATURE [Part::Extrusion] Extrude148  label="bounds_right"
  Base = -> path44149_5_005
  Dir = (0,0,1)
  DirMode = 0
  FaceMakerClass = Part::FaceMakerBullseye
  LengthFwd = 3.8
  LengthRev = 0
  Solid = true
  Symmetric = false
FEATURE [Part::Feature] path010
  Placement = pos=(71.4721,-85.7664,0) rot=(0,0,1;0rad)
  shape: bbox 6.624 x 7.244 x 2e-07 mm, 0 faces, 0 solids (baked)
FEATURE [Part::Extrusion] Extrude150
  Base = -> path010
  Dir = (0,0,1)
  DirMode = 0
  FaceMakerClass = Part::FaceMakerBullseye
  LengthFwd = 1
  LengthRev = 0
  Solid = true
  Symmetric = false
FEATURE [Part::Feature] path9_010
  Placement = pos=(71.4721,-121.766,0) rot=(0,0,1;0rad)
  shape: bbox 6.624 x 7.244 x 2e-07 mm, 0 faces, 0 solids (baked)
FEATURE [Part::Extrusion] Extrude151
  Base = -> path9_010
  Dir = (0,0,1)
  DirMode = 0
  FaceMakerClass = Part::FaceMakerBullseye
  LengthFwd = 1
  LengthRev = 0
  Solid = true
  Symmetric = false
FEATURE [Part::Feature] path9_92_7_010
  Placement = pos=(125.472,-60.2664,0) rot=(0,0,1;0rad)
  shape: bbox 6.624 x 7.244 x 2e-07 mm, 0 faces, 0 solids (baked)
FEATURE [Part::Extrusion] Extrude152
  Base = -> path9_92_7_010
  Dir = (0,0,1)
  DirMode = 0
  FaceMakerClass = Part::FaceMakerBullseye
  LengthFwd = 1
  LengthRev = 0
  Solid = true
  Symmetric = false
FEATURE [Part::Feature] path9_92_7_9_010
  Placement = pos=(144.472,-60.2664,0) rot=(0,0,1;0rad)
  shape: bbox 6.624 x 7.244 x 2e-07 mm, 0 faces, 0 solids (baked)
FEATURE [Part::Extrusion] Extrude153
  Base = -> path9_92_7_9_010
  Dir = (0,0,1)
  DirMode = 0
  FaceMakerClass = Part::FaceMakerBullseye
  LengthFwd = 1
  LengthRev = 0
  Solid = true
  Symmetric = false
FEATURE [Part::Feature] path9_92_7_9_9_005
  Placement = pos=(210.001,-67.2664,0) rot=(0,0,1;0rad)
  shape: bbox 6.624 x 7.244 x 2e-07 mm, 0 faces, 0 solids (baked)
FEATURE [Part::Extrusion] Extrude154
  Base = -> path9_92_7_9_9_005
  Dir = (0,0,1)
  DirMode = 0
  FaceMakerClass = Part::FaceMakerBullseye
  LengthFwd = 1
  LengthRev = 0
  Solid = true
  Symmetric = false
FEATURE [Part::Feature] path9_92_7_9_9_4_4_8_003
  Placement = pos=(199.796,-154.63,0) rot=(0,0,1;0rad)
  shape: bbox 6.624 x 7.244 x 2e-07 mm, 0 faces, 0 solids (baked)
FEATURE [Part::Extrusion] Extrude156
  Base = -> path9_92_7_9_9_4_4_8_003
  Dir = (0,0,1)
  DirMode = 0
  FaceMakerClass = Part::FaceMakerBullseye
  LengthFwd = 1
  LengthRev = 0
  Solid = true
  Symmetric = false
FEATURE [Part::Feature] path9_92_7_9_9_4_4_8_2_005
  Placement = pos=(133.155,-139.413,0) rot=(0,0,1;0rad)
  shape: bbox 6.624 x 7.244 x 2e-07 mm, 0 faces, 0 solids (baked)
FEATURE [Part::Extrusion] Extrude157
  Base = -> path9_92_7_9_9_4_4_8_2_005
  Dir = (0,0,1)
  DirMode = 0
  FaceMakerClass = Part::FaceMakerBullseye
  LengthFwd = 1
  LengthRev = 0
  Solid = true
  Symmetric = false
FEATURE [Part::Feature] path9_92_7_9_9_4_4_8_2_4_007
  Placement = pos=(182.228,-67.2664,0) rot=(0,0,1;0rad)
  shape: bbox 6.624 x 7.244 x 2e-07 mm, 0 faces, 0 solids (baked)
FEATURE [Part::Extrusion] Extrude159
  Base = -> path9_92_7_9_9_4_4_8_2_4_007
  Dir = (0,0,1)
  DirMode = 0
  FaceMakerClass = Part::FaceMakerBullseye
  LengthFwd = 1
  LengthRev = 0
  Solid = true
  Symmetric = false
FEATURE [Part::Feature] path9_92_7_9_9_4_4_8_2_4_008
  Placement = pos=(169.885,-138.433,0) rot=(0,0,1;0rad)
  shape: bbox 6.624 x 7.244 x 2e-07 mm, 0 faces, 0 solids (baked)
FEATURE [Part::Extrusion] Extrude158
  Base = -> path9_92_7_9_9_4_4_8_2_4_008
  Dir = (0,0,1)
  DirMode = 0
  FaceMakerClass = Part::FaceMakerBullseye
  LengthFwd = 1
  LengthRev = 0
  Solid = true
  Symmetric = false
FEATURE [Part::Feature] path9_9_006
  Placement = pos=(89.4721,-130.266,0) rot=(0,0,1;0rad)
  shape: bbox 6.624 x 7.244 x 2e-07 mm, 0 faces, 0 solids (baked)
FEATURE [Part::Extrusion] Extrude155
  Base = -> path9_9_006
  Dir = (0,0,1)
  DirMode = 0
  FaceMakerClass = Part::FaceMakerBullseye
  LengthFwd = 1
  LengthRev = 0
  Solid = true
  Symmetric = false
FEATURE [Part::MultiFuse] Fusion002  label="feet_right"
  Shapes = -> [Extrude150,Extrude151,Extrude152,Extrude153,Extrude154,Extrude155,Extrude156,Extrude157,Extrude158,Extrude159]
FEATURE [Part::Feature] path52377_09_3_1_8_87_9
  Placement = pos=(-112.198,-129.883,0) rot=(0,0,1;0rad)
  shape: bbox 1.877 x 2.052 x 2e-07 mm, 0 faces, 0 solids (baked)
FEATURE [Part::Feature] path52401_71_2_4_9_8_2
  Placement = pos=(-111.698,-133.683,0) rot=(0,0,1;0rad)
  shape: bbox 2.208 x 2.415 x 2e-07 mm, 0 faces, 0 solids (baked)
FEATURE [Part::Feature] path52401_7_8_1_8_2_30_6
  Placement = pos=(-106.698,-135.783,0) rot=(0,0,1;0rad)
  shape: bbox 2.208 x 2.415 x 2e-07 mm, 0 faces, 0 solids (baked)
FEATURE [Part::Feature] path52377_0_5_0_4_2_3_6
  Placement = pos=(-101.198,-129.883,0) rot=(0,0,1;0rad)
  shape: bbox 1.877 x 2.052 x 2e-07 mm, 0 faces, 0 solids (baked)
FEATURE [Part::Feature] path52456_0_5_5_7_86_8
  Placement = pos=(-106.698,-129.883,0) rot=(0,0,1;0rad)
  shape: bbox 3.787 x 4.141 x 2e-07 mm, 0 faces, 0 solids (baked)
FEATURE [Part::Feature] path52377_09_3_1_8_8_2_0
  Placement = pos=(-112.198,-112.884,0) rot=(0,0,1;0rad)
  shape: bbox 1.877 x 2.052 x 2e-07 mm, 0 faces, 0 solids (baked)
FEATURE [Part::Feature] path52401_71_2_4_9_4_5_7
  Placement = pos=(-111.698,-116.684,0) rot=(0,0,1;0rad)
  shape: bbox 2.208 x 2.415 x 2e-07 mm, 0 faces, 0 solids (baked)
FEATURE [Part::Feature] path52401_7_8_1_8_2_3_11_7
  Placement = pos=(-106.698,-118.784,0) rot=(0,0,1;0rad)
  shape: bbox 2.208 x 2.415 x 2e-07 mm, 0 faces, 0 solids (baked)
FEATURE [Part::Feature] path52377_0_5_0_4_2_4_5_9
  Placement = pos=(-101.198,-112.884,0) rot=(0,0,1;0rad)
  shape: bbox 1.877 x 2.052 x 2e-07 mm, 0 faces, 0 solids (baked)
FEATURE [Part::Feature] path52456_0_5_5_7_7_0_9
  Placement = pos=(-106.698,-112.884,0) rot=(0,0,1;0rad)
  shape: bbox 3.787 x 4.141 x 2e-07 mm, 0 faces, 0 solids (baked)
FEATURE [Part::Feature] path52377_09_3_1_8_2_3_2
  Placement = pos=(-130.198,-121.383,0) rot=(0,0,1;0rad)
  shape: bbox 1.877 x 2.052 x 2e-07 mm, 0 faces, 0 solids (baked)
FEATURE [Part::Feature] path52401_71_2_4_9_2_39_0
  Placement = pos=(-129.698,-125.183,0) rot=(0,0,1;0rad)
  shape: bbox 2.208 x 2.415 x 2e-07 mm, 0 faces, 0 solids (baked)
FEATURE [Part::Feature] path52401_7_8_1_8_2_31_2_2
  Placement = pos=(-124.698,-127.283,0) rot=(0,0,1;0rad)
  shape: bbox 2.208 x 2.415 x 2e-07 mm, 0 faces, 0 solids (baked)
FEATURE [Part::Feature] path52377_0_5_0_4_2_41_1_6
  Placement = pos=(-119.198,-121.383,0) rot=(0,0,1;0rad)
  shape: bbox 1.877 x 2.052 x 2e-07 mm, 0 faces, 0 solids (baked)
FEATURE [Part::Feature] path52456_0_5_5_7_4_2_7
  Placement = pos=(-124.698,-121.383,0) rot=(0,0,1;0rad)
  shape: bbox 3.787 x 4.141 x 2e-07 mm, 0 faces, 0 solids (baked)
FEATURE [Part::Feature] path52377_09_3_1_8_2_4_7_4
  Placement = pos=(-130.198,-138.383,0) rot=(0,0,1;0rad)
  shape: bbox 1.877 x 2.052 x 2e-07 mm, 0 faces, 0 solids (baked)
FEATURE [Part::Feature] path52401_71_2_4_9_2_9_8_3
  Placement = pos=(-129.698,-142.183,0) rot=(0,0,1;0rad)
  shape: bbox 2.208 x 2.415 x 2e-07 mm, 0 faces, 0 solids (baked)
FEATURE [Part::Feature] path52401_7_8_1_8_2_31_5_4_3
  Placement = pos=(-124.698,-144.283,0) rot=(0,0,1;0rad)
  shape: bbox 2.208 x 2.415 x 2e-07 mm, 0 faces, 0 solids (baked)
FEATURE [Part::Feature] path52377_0_5_0_4_2_41_0_0_8
  Placement = pos=(-119.198,-138.383,0) rot=(0,0,1;0rad)
  shape: bbox 1.877 x 2.052 x 2e-07 mm, 0 faces, 0 solids (baked)
FEATURE [Part::Feature] path52456_0_5_5_7_4_4_1_2
  Placement = pos=(-124.698,-138.383,0) rot=(0,0,1;0rad)
  shape: bbox 3.787 x 4.141 x 2e-07 mm, 0 faces, 0 solids (baked)
FEATURE [Part::Feature] path52377_09_3_1_8_8_0_3_5
  Placement = pos=(-130.198,-104.384,0) rot=(0,0,1;0rad)
  shape: bbox 1.877 x 2.052 x 2e-07 mm, 0 faces, 0 solids (baked)
FEATURE [Part::Feature] path52401_71_2_4_9_4_2_0_8
  Placement = pos=(-129.698,-108.184,0) rot=(0,0,1;0rad)
  shape: bbox 2.208 x 2.415 x 2e-07 mm, 0 faces, 0 solids (baked)
FEATURE [Part::Feature] path52401_7_8_1_8_2_3_5_0_1
  Placement = pos=(-124.698,-110.284,0) rot=(0,0,1;0rad)
  shape: bbox 2.208 x 2.415 x 2e-07 mm, 0 faces, 0 solids (baked)
FEATURE [Part::Feature] path52377_0_5_0_4_2_4_4_3_3
  Placement = pos=(-119.198,-104.384,0) rot=(0,0,1;0rad)
  shape: bbox 1.877 x 2.052 x 2e-07 mm, 0 faces, 0 solids (baked)
FEATURE [Part::Feature] path52456_0_5_5_7_7_7_7_4
  Placement = pos=(-124.698,-104.384,0) rot=(0,0,1;0rad)
  shape: bbox 3.787 x 4.141 x 2e-07 mm, 0 faces, 0 solids (baked)
FEATURE [Part::Feature] path52377_09_3_1_8_2_9_7_8
  Placement = pos=(-148.198,-109.383,0) rot=(0,0,1;0rad)
  shape: bbox 1.877 x 2.052 x 2e-07 mm, 0 faces, 0 solids (baked)
FEATURE [Part::Feature] path52401_71_2_4_9_2_6_0_6
  Placement = pos=(-147.698,-113.183,0) rot=(0,0,1;0rad)
  shape: bbox 2.208 x 2.415 x 2e-07 mm, 0 faces, 0 solids (baked)
FEATURE [Part::Feature] path52401_7_8_1_8_2_31_56_74_0
  Placement = pos=(-142.698,-115.283,0) rot=(0,0,1;0rad)
  shape: bbox 2.208 x 2.415 x 2e-07 mm, 0 faces, 0 solids (baked)
FEATURE [Part::Feature] path52377_0_5_0_4_2_41_4_91_1
  Placement = pos=(-137.198,-109.383,0) rot=(0,0,1;0rad)
  shape: bbox 1.877 x 2.052 x 2e-07 mm, 0 faces, 0 solids (baked)
FEATURE [Part::Feature] path52456_0_5_5_7_4_40_0_2
  Placement = pos=(-142.698,-109.383,0) rot=(0,0,1;0rad)
  shape: bbox 3.787 x 4.141 x 2e-07 mm, 0 faces, 0 solids (baked)
FEATURE [Part::Feature] path52377_09_3_1_8_2_4_0_1_3
  Placement = pos=(-148.198,-126.383,0) rot=(0,0,1;0rad)
  shape: bbox 1.877 x 2.052 x 2e-07 mm, 0 faces, 0 solids (baked)
FEATURE [Part::Feature] path52401_71_2_4_9_2_9_9_55_5
  Placement = pos=(-147.698,-130.183,0) rot=(0,0,1;0rad)
  shape: bbox 2.208 x 2.415 x 2e-07 mm, 0 faces, 0 solids (baked)
FEATURE [Part::Feature] path52401_7_8_1_8_2_31_5_9_4_8
  Placement = pos=(-142.698,-132.283,0) rot=(0,0,1;0rad)
  shape: bbox 2.208 x 2.415 x 2e-07 mm, 0 faces, 0 solids (baked)
FEATURE [Part::Feature] path52377_0_5_0_4_2_41_0_4_8_5
  Placement = pos=(-137.198,-126.383,0) rot=(0,0,1;0rad)
  shape: bbox 1.877 x 2.052 x 2e-07 mm, 0 faces, 0 solids (baked)
FEATURE [Part::Feature] path52456_0_5_5_7_4_4_8_02_7
  Placement = pos=(-142.698,-126.383,0) rot=(0,0,1;0rad)
  shape: bbox 3.787 x 4.141 x 2e-07 mm, 0 faces, 0 solids (baked)
FEATURE [Part::Feature] path52377_09_3_1_8_8_0_4_7_0
  Placement = pos=(-148.198,-92.3836,0) rot=(0,0,1;0rad)
  shape: bbox 1.877 x 2.052 x 2e-07 mm, 0 faces, 0 solids (baked)
FEATURE [Part::Feature] path52401_71_2_4_9_4_2_2_1_9
  Placement = pos=(-147.698,-96.1835,0) rot=(0,0,1;0rad)
  shape: bbox 2.208 x 2.415 x 2e-07 mm, 0 faces, 0 solids (baked)
FEATURE [Part::Feature] path52401_7_8_1_8_2_3_5_3_8_2
  Placement = pos=(-142.698,-98.2836,0) rot=(0,0,1;0rad)
  shape: bbox 2.208 x 2.415 x 2e-07 mm, 0 faces, 0 solids (baked)
FEATURE [Part::Feature] path52377_0_5_0_4_2_4_4_8_3_2
  Placement = pos=(-137.198,-92.3836,0) rot=(0,0,1;0rad)
  shape: bbox 1.877 x 2.052 x 2e-07 mm, 0 faces, 0 solids (baked)
FEATURE [Part::Feature] path52456_0_5_5_7_7_7_1_3_6
  Placement = pos=(-142.698,-92.3836,0) rot=(0,0,1;0rad)
  shape: bbox 3.787 x 4.141 x 2e-07 mm, 0 faces, 0 solids (baked)
FEATURE [Part::Feature] path52377_09_3_1_8_2_9_5_3_6
  Placement = pos=(-166.198,-104.383,0) rot=(0,0,1;0rad)
  shape: bbox 1.877 x 2.052 x 2e-07 mm, 0 faces, 0 solids (baked)
FEATURE [Part::Feature] path52401_71_2_4_9_2_6_3_64_9
  Placement = pos=(-165.698,-108.183,0) rot=(0,0,1;0rad)
  shape: bbox 2.208 x 2.415 x 2e-07 mm, 0 faces, 0 solids (baked)
FEATURE [Part::Feature] path52401_7_8_1_8_2_31_56_1_9_8
  Placement = pos=(-160.698,-110.283,0) rot=(0,0,1;0rad)
  shape: bbox 2.208 x 2.415 x 2e-07 mm, 0 faces, 0 solids (baked)
FEATURE [Part::Feature] path52377_0_5_0_4_2_41_4_8_1_3
  Placement = pos=(-155.198,-104.383,0) rot=(0,0,1;0rad)
  shape: bbox 1.877 x 2.052 x 2e-07 mm, 0 faces, 0 solids (baked)
FEATURE [Part::Feature] path52456_0_5_5_7_4_40_5_0_6
  Placement = pos=(-160.698,-104.383,0) rot=(0,0,1;0rad)
  shape: bbox 3.787 x 4.141 x 2e-07 mm, 0 faces, 0 solids (baked)
FEATURE [Part::Feature] path52377_09_3_1_8_2_4_0_5_8_4
  Placement = pos=(-166.198,-121.383,0) rot=(0,0,1;0rad)
  shape: bbox 1.877 x 2.052 x 2e-07 mm, 0 faces, 0 solids (baked)
FEATURE [Part::Feature] path52401_71_2_4_9_2_9_9_5_64_7
  Placement = pos=(-165.698,-125.183,0) rot=(0,0,1;0rad)
  shape: bbox 2.208 x 2.415 x 2e-07 mm, 0 faces, 0 solids (baked)
FEATURE [Part::Feature] path52401_7_8_1_8_2_31_5_9_9_9_3
  Placement = pos=(-160.698,-127.283,0) rot=(0,0,1;0rad)
  shape: bbox 2.208 x 2.415 x 2e-07 mm, 0 faces, 0 solids (baked)
FEATURE [Part::Feature] path52377_0_5_0_4_2_41_0_4_1_4_0
  Placement = pos=(-155.198,-121.383,0) rot=(0,0,1;0rad)
  shape: bbox 1.877 x 2.052 x 2e-07 mm, 0 faces, 0 solids (baked)
FEATURE [Part::Feature] path52456_0_5_5_7_4_4_8_5_4_4
  Placement = pos=(-160.698,-121.383,0) rot=(0,0,1;0rad)
  shape: bbox 3.787 x 4.141 x 2e-07 mm, 0 faces, 0 solids (baked)
FEATURE [Part::Feature] path52377_09_3_1_8_8_0_4_5_6_9
  Placement = pos=(-166.198,-87.3836,0) rot=(0,0,1;0rad)
  shape: bbox 1.877 x 2.052 x 2e-07 mm, 0 faces, 0 solids (baked)
FEATURE [Part::Feature] path52401_71_2_4_9_4_2_2_8_5_1
  Placement = pos=(-165.698,-91.1835,0) rot=(0,0,1;0rad)
  shape: bbox 2.208 x 2.415 x 2e-07 mm, 0 faces, 0 solids (baked)
FEATURE [Part::Feature] path52401_7_8_1_8_2_3_5_3_4_2_3
  Placement = pos=(-160.698,-93.2836,0) rot=(0,0,1;0rad)
  shape: bbox 2.208 x 2.415 x 2e-07 mm, 0 faces, 0 solids (baked)
FEATURE [Part::Feature] path52377_0_5_0_4_2_4_4_8_9_1_6
  Placement = pos=(-155.198,-87.3836,0) rot=(0,0,1;0rad)
  shape: bbox 1.877 x 2.052 x 2e-07 mm, 0 faces, 0 solids (baked)
FEATURE [Part::Feature] path52456_0_5_5_7_7_7_1_7_8_9
  Placement = pos=(-160.698,-87.3836,0) rot=(0,0,1;0rad)
  shape: bbox 3.787 x 4.141 x 2e-07 mm, 0 faces, 0 solids (baked)
FEATURE [Part::Feature] path52377_09_3_1_8_2_9_5_4_8_4
  Placement = pos=(-184.198,-109.383,0) rot=(0,0,1;0rad)
  shape: bbox 1.877 x 2.052 x 2e-07 mm, 0 faces, 0 solids (baked)
FEATURE [Part::Feature] path52401_71_2_4_9_2_6_3_6_9_9
  Placement = pos=(-183.698,-113.183,0) rot=(0,0,1;0rad)
  shape: bbox 2.208 x 2.415 x 2e-07 mm, 0 faces, 0 solids (baked)
FEATURE [Part::Feature] path52401_7_8_1_8_2_31_56_1_3_7_7
  Placement = pos=(-178.698,-115.283,0) rot=(0,0,1;0rad)
  shape: bbox 2.208 x 2.415 x 2e-07 mm, 0 faces, 0 solids (baked)
FEATURE [Part::Feature] path52377_0_5_0_4_2_41_4_8_8_6_8
  Placement = pos=(-173.198,-109.383,0) rot=(0,0,1;0rad)
  shape: bbox 1.877 x 2.052 x 2e-07 mm, 0 faces, 0 solids (baked)
FEATURE [Part::Feature] path52456_0_5_5_7_4_40_5_1_45_0
  Placement = pos=(-178.698,-109.383,0) rot=(0,0,1;0rad)
  shape: bbox 3.787 x 4.141 x 2e-07 mm, 0 faces, 0 solids (baked)
FEATURE [Part::Feature] path52377_09_3_1_8_2_4_0_5_0_4_8
  Placement = pos=(-184.198,-126.383,0) rot=(0,0,1;0rad)
  shape: bbox 1.877 x 2.052 x 2e-07 mm, 0 faces, 0 solids (baked)
FEATURE [Part::Feature] path52401_71_2_4_9_2_9_9_5_6_8_4
  Placement = pos=(-183.698,-130.183,0) rot=(0,0,1;0rad)
  shape: bbox 2.208 x 2.415 x 2e-07 mm, 0 faces, 0 solids (baked)
FEATURE [Part::Feature] path52401_7_8_1_8_2_31_5_9_9_0_0_2
  Placement = pos=(-178.698,-132.283,0) rot=(0,0,1;0rad)
  shape: bbox 2.208 x 2.415 x 2e-07 mm, 0 faces, 0 solids (baked)
FEATURE [Part::Feature] path52377_0_5_0_4_2_41_0_4_1_8_44_4
  Placement = pos=(-173.198,-126.383,0) rot=(0,0,1;0rad)
  shape: bbox 1.877 x 2.052 x 2e-07 mm, 0 faces, 0 solids (baked)
FEATURE [Part::Feature] path52456_0_5_5_7_4_4_8_5_8_8_3
  Placement = pos=(-178.698,-126.383,0) rot=(0,0,1;0rad)
  shape: bbox 3.787 x 4.141 x 2e-07 mm, 0 faces, 0 solids (baked)
FEATURE [Part::Feature] path52377_09_3_1_8_8_0_4_5_8_91_9
  Placement = pos=(-184.198,-92.3836,0) rot=(0,0,1;0rad)
  shape: bbox 1.877 x 2.052 x 2e-07 mm, 0 faces, 0 solids (baked)
FEATURE [Part::Feature] path52401_71_2_4_9_4_2_2_8_7_5_0
  Placement = pos=(-183.698,-96.1835,0) rot=(0,0,1;0rad)
  shape: bbox 2.208 x 2.415 x 2e-07 mm, 0 faces, 0 solids (baked)
FEATURE [Part::Feature] path52401_7_8_1_8_2_3_5_3_4_4_44_4
  Placement = pos=(-178.698,-98.2836,0) rot=(0,0,1;0rad)
  shape: bbox 2.208 x 2.415 x 2e-07 mm, 0 faces, 0 solids (baked)
FEATURE [Part::Feature] path52377_0_5_0_4_2_4_4_8_9_2_9_3
  Placement = pos=(-173.198,-92.3836,0) rot=(0,0,1;0rad)
  shape: bbox 1.877 x 2.052 x 2e-07 mm, 0 faces, 0 solids (baked)
FEATURE [Part::Feature] path52456_0_5_5_7_7_7_1_7_0_2_7
  Placement = pos=(-178.698,-92.3836,0) rot=(0,0,1;0rad)
  shape: bbox 3.787 x 4.141 x 2e-07 mm, 0 faces, 0 solids (baked)
FEATURE [Part::Feature] path52377_09_3_1_8_2_9_5_4_9_5_7
  Placement = pos=(-202.198,-111.383,0) rot=(0,0,1;0rad)
  shape: bbox 1.877 x 2.052 x 2e-07 mm, 0 faces, 0 solids (baked)
FEATURE [Part::Feature] path52401_71_2_4_9_2_6_3_6_8_5_8
  Placement = pos=(-201.698,-115.183,0) rot=(0,0,1;0rad)
  shape: bbox 2.208 x 2.415 x 2e-07 mm, 0 faces, 0 solids (baked)
FEATURE [Part::Feature] path52401_7_8_1_8_2_31_56_1_3_0_2_9
  Placement = pos=(-196.698,-117.283,0) rot=(0,0,1;0rad)
  shape: bbox 2.208 x 2.415 x 2e-07 mm, 0 faces, 0 solids (baked)
FEATURE [Part::Feature] path52377_0_5_0_4_2_41_4_8_8_0_5_5
  Placement = pos=(-191.198,-111.383,0) rot=(0,0,1;0rad)
  shape: bbox 1.877 x 2.052 x 2e-07 mm, 0 faces, 0 solids (baked)
FEATURE [Part::Feature] path52456_0_5_5_7_4_40_5_1_5_56_6
  Placement = pos=(-196.698,-111.383,0) rot=(0,0,1;0rad)
  shape: bbox 3.787 x 4.141 x 2e-07 mm, 0 faces, 0 solids (baked)
FEATURE [Part::Feature] path52377_09_3_1_8_2_4_0_5_0_2_7_9
  Placement = pos=(-202.198,-128.383,0) rot=(0,0,1;0rad)
  shape: bbox 1.877 x 2.052 x 2e-07 mm, 0 faces, 0 solids (baked)
FEATURE [Part::Feature] path52401_71_2_4_9_2_9_9_5_6_2_6_5
  Placement = pos=(-201.698,-132.183,0) rot=(0,0,1;0rad)
  shape: bbox 2.208 x 2.415 x 2e-07 mm, 0 faces, 0 solids (baked)
FEATURE [Part::Feature] path52401_7_8_1_8_2_31_5_9_9_0_7_2_4
  Placement = pos=(-196.698,-134.283,0) rot=(0,0,1;0rad)
  shape: bbox 2.208 x 2.415 x 2e-07 mm, 0 faces, 0 solids (baked)
FEATURE [Part::Feature] path52377_0_5_0_4_2_41_0_4_1_8_4_4_5
  Placement = pos=(-191.198,-128.383,0) rot=(0,0,1;0rad)
  shape: bbox 1.877 x 2.052 x 2e-07 mm, 0 faces, 0 solids (baked)
FEATURE [Part::Feature] path52456_0_5_5_7_4_4_8_5_8_0_3_1
  Placement = pos=(-196.698,-128.383,0) rot=(0,0,1;0rad)
  shape: bbox 3.787 x 4.141 x 2e-07 mm, 0 faces, 0 solids (baked)
FEATURE [Part::Feature] path52377_09_3_1_8_8_0_4_5_8_9_1_3
  Placement = pos=(-202.198,-94.3836,0) rot=(0,0,1;0rad)
  shape: bbox 1.877 x 2.052 x 2e-07 mm, 0 faces, 0 solids (baked)
FEATURE [Part::Feature] path52401_71_2_4_9_4_2_2_8_7_6_2_4
  Placement = pos=(-201.698,-98.1836,0) rot=(0,0,1;0rad)
  shape: bbox 2.208 x 2.415 x 2e-07 mm, 0 faces, 0 solids (baked)
FEATURE [Part::Feature] path52401_7_8_1_8_2_3_5_3_4_4_8_8_9
  Placement = pos=(-196.698,-100.284,0) rot=(0,0,1;0rad)
  shape: bbox 2.208 x 2.415 x 2e-07 mm, 0 faces, 0 solids (baked)
FEATURE [Part::Feature] path52377_0_5_0_4_2_4_4_8_9_2_0_5_5
  Placement = pos=(-191.198,-94.3836,0) rot=(0,0,1;0rad)
  shape: bbox 1.877 x 2.052 x 2e-07 mm, 0 faces, 0 solids (baked)
FEATURE [Part::Feature] path52456_0_5_5_7_7_7_1_7_0_0_6_4
  Placement = pos=(-196.698,-94.3836,0) rot=(0,0,1;0rad)
  shape: bbox 3.787 x 4.141 x 2e-07 mm, 0 faces, 0 solids (baked)
FEATURE [Part::Feature] path37937_8_6
  shape: bbox 1.702 x 2 x 2e-07 mm, 0 faces, 0 solids (baked)
FEATURE [Part::Feature] path37931_6_7
  shape: bbox 1.7 x 2 x 2e-07 mm, 0 faces, 0 solids (baked)
FEATURE [Part::Feature] path37321_9_5
  shape: bbox 2.002 x 1.603 x 2e-07 mm, 0 faces, 0 solids (baked)
FEATURE [Part::Feature] path37327_3_6
  shape: bbox 2.002 x 1.601 x 2e-07 mm, 0 faces, 0 solids (baked)
FEATURE [Part::Feature] path37329_6_1
  shape: bbox 2.002 x 1.603 x 2e-07 mm, 0 faces, 0 solids (baked)
FEATURE [Part::Feature] path37333_00_0
  shape: bbox 2.002 x 1.603 x 2e-07 mm, 0 faces, 0 solids (baked)
FEATURE [Part::Feature] circle37301_1_8
  Placement = pos=(227.782,-141.699,0) rot=(0,0,1;0rad)
  shape: bbox 0.8832 x 0.9658 x 2e-07 mm, 0 faces, 0 solids (baked)
FEATURE [Part::Feature] circle37295_7_4
  Placement = pos=(234.782,-141.699,0) rot=(0,0,1;0rad)
  shape: bbox 0.8832 x 0.9658 x 2e-07 mm, 0 faces, 0 solids (baked)
FEATURE [Part::Feature] rect117948_11_2
  shape: bbox 1.7 x 49.96 x 2e-07 mm, 0 faces, 0 solids (baked)
FEATURE [Part::Feature] rect117948_2_00_4
  shape: bbox 1.7 x 49.96 x 2e-07 mm, 0 faces, 0 solids (baked)
FEATURE [Part::Feature] path61609_4_5_7_9_4_80_0_4
  shape: bbox 15 x 7.701 x 2e-07 mm, 0 faces, 0 solids (baked)
FEATURE [Part::Feature] path61609_4_5_7_9_4_80_0_3_84
  shape: bbox 15 x 7.701 x 2e-07 mm, 0 faces, 0 solids (baked)
FEATURE [Part::Feature] path61609_4_5_7_9_4_80_0_8_5
  shape: bbox 15 x 7.701 x 2e-07 mm, 0 faces, 0 solids (baked)
FEATURE [Part::Feature] path61609_4_5_7_9_4_80_0_3_8_08
  shape: bbox 15 x 7.701 x 2e-07 mm, 0 faces, 0 solids (baked)
FEATURE [Part::Feature] path61609_4_5_7_9_4_80_0_3_8_6_37
  shape: bbox 15 x 7.701 x 2e-07 mm, 0 faces, 0 solids (baked)
FEATURE [Part::Feature] path61609_4_5_7_9_4_80_0_8_3_4
  shape: bbox 15 x 7.701 x 2e-07 mm, 0 faces, 0 solids (baked)
FEATURE [Part::Feature] path61609_4_5_7_9_4_80_0_3_8_9_8
  shape: bbox 15 x 7.701 x 2e-07 mm, 0 faces, 0 solids (baked)
FEATURE [Part::Feature] path61609_4_5_7_9_4_80_0_3_8_6_1_7
  shape: bbox 15 x 7.701 x 2e-07 mm, 0 faces, 0 solids (baked)
FEATURE [Part::Feature] path61609_4_5_7_9_4_80_0_8_7_4
  shape: bbox 15 x 7.701 x 2e-07 mm, 0 faces, 0 solids (baked)
FEATURE [Part::Feature] path61609_4_5_7_9_4_80_0_3_8_91_7
  shape: bbox 15 x 7.701 x 2e-07 mm, 0 faces, 0 solids (baked)
FEATURE [Part::Feature] path61609_4_5_7_9_4_80_0_3_8_6_3_5
  shape: bbox 15 x 7.701 x 2e-07 mm, 0 faces, 0 solids (baked)
FEATURE [Part::Feature] path61609_4_5_7_9_4_80_0_8_8_0
  shape: bbox 15 x 7.701 x 2e-07 mm, 0 faces, 0 solids (baked)
FEATURE [Part::Feature] path61609_4_5_7_9_4_80_0_3_8_0_5
  shape: bbox 15 x 7.701 x 2e-07 mm, 0 faces, 0 solids (baked)
FEATURE [Part::Feature] path61609_4_5_7_9_4_80_0_3_8_6_7_1
  shape: bbox 15 x 7.701 x 2e-07 mm, 0 faces, 0 solids (baked)
FEATURE [Part::Feature] path61609_4_5_7_9_4_80_0_8_2_8
  shape: bbox 15 x 7.701 x 2e-07 mm, 0 faces, 0 solids (baked)
FEATURE [Part::Feature] path61609_4_5_7_9_4_80_0_3_8_60_1
  shape: bbox 15 x 7.701 x 2e-07 mm, 0 faces, 0 solids (baked)
FEATURE [Part::Feature] path61609_4_5_7_9_4_80_0_3_8_6_4_3
  shape: bbox 15 x 7.701 x 2e-07 mm, 0 faces, 0 solids (baked)
FEATURE [Part::Feature] path52377_09_3_5_7_6_7_3
  Placement = pos=(-143.035,-172.587,0) rot=(0,0,1;0rad)
  shape: bbox 2.028 x 2.027 x 2e-07 mm, 0 faces, 0 solids (baked)
FEATURE [Part::Feature] path52401_71_2_5_9_2_77_3
  Placement = pos=(-142.535,-176.387,0) rot=(0,0,1;0rad)
  shape: bbox 2.386 x 2.384 x 2e-07 mm, 0 faces, 0 solids (baked)
FEATURE [Part::Feature] path52401_7_8_1_1_7_3_9_0
  Placement = pos=(-137.535,-178.487,0) rot=(0,0,1;0rad)
  shape: bbox 2.386 x 2.384 x 2e-07 mm, 0 faces, 0 solids (baked)
FEATURE [Part::Feature] path52377_0_5_0_1_9_1_5_5
  Placement = pos=(-132.035,-172.587,0) rot=(0,0,1;0rad)
  shape: bbox 2.028 x 2.027 x 2e-07 mm, 0 faces, 0 solids (baked)
FEATURE [Part::Feature] path52456_0_5_2_2_2_3_5
  Placement = pos=(-137.535,-172.587,0) rot=(0,0,1;0rad)
  shape: bbox 4.091 x 4.089 x 2e-07 mm, 0 faces, 0 solids (baked)
FEATURE [Part::Feature] path52377_09_3_5_7_6_0_0_2
  Placement = pos=(-279.563,-2.13117,0) rot=(0,0,1;0rad)
  shape: bbox 2.046 x 1.999 x 2e-07 mm, 0 faces, 0 solids (baked)
FEATURE [Part::Feature] path52401_71_2_5_9_2_7_5_4
  Placement = pos=(-279.063,-5.93117,0) rot=(0,0,1;0rad)
  shape: bbox 2.407 x 2.351 x 2e-07 mm, 0 faces, 0 solids (baked)
FEATURE [Part::Feature] path52401_7_8_1_1_7_3_8_4_4
  Placement = pos=(-274.063,-8.03117,0) rot=(0,0,1;0rad)
  shape: bbox 2.407 x 2.351 x 2e-07 mm, 0 faces, 0 solids (baked)
FEATURE [Part::Feature] path52377_0_5_0_1_9_1_0_6_9
  Placement = pos=(-268.563,-2.13117,0) rot=(0,0,1;0rad)
  shape: bbox 2.046 x 1.999 x 2e-07 mm, 0 faces, 0 solids (baked)
FEATURE [Part::Feature] path52456_0_5_2_2_2_9_9_3
  Placement = pos=(-274.063,-2.13117,0) rot=(0,0,1;0rad)
  shape: bbox 4.128 x 4.033 x 2e-07 mm, 0 faces, 0 solids (baked)
FEATURE [Part::Feature] path52377_09_3_5_7_6_6_7_9
  Placement = pos=(-249.546,-70.6289,0) rot=(0,0,1;0rad)
  shape: bbox 2.026 x 2.027 x 2e-07 mm, 0 faces, 0 solids (baked)
FEATURE [Part::Feature] path52401_71_2_5_9_2_1_4_5
  Placement = pos=(-249.046,-74.4289,0) rot=(0,0,1;0rad)
  shape: bbox 2.384 x 2.385 x 2e-07 mm, 0 faces, 0 solids (baked)
FEATURE [Part::Feature] path52401_7_8_1_1_7_3_1_9_1
  Placement = pos=(-244.046,-76.5289,0) rot=(0,0,1;0rad)
  shape: bbox 2.384 x 2.385 x 2e-07 mm, 0 faces, 0 solids (baked)
FEATURE [Part::Feature] path52377_0_5_0_1_9_1_3_9_3
  Placement = pos=(-238.546,-70.6289,0) rot=(0,0,1;0rad)
  shape: bbox 2.026 x 2.027 x 2e-07 mm, 0 faces, 0 solids (baked)
FEATURE [Part::Feature] path52456_0_5_2_2_2_5_8_5
  Placement = pos=(-244.046,-70.6289,0) rot=(0,0,1;0rad)
  shape: bbox 4.088 x 4.091 x 2e-07 mm, 0 faces, 0 solids (baked)
FEATURE [Part::Feature] path52377_09_3_5_7_6_4_7_2
  Placement = pos=(-202.897,-128.725,0) rot=(0,0,1;0rad)
  shape: bbox 1.997 x 2.046 x 2e-07 mm, 0 faces, 0 solids (baked)
FEATURE [Part::Feature] path52401_71_2_5_9_2_8_0_6
  Placement = pos=(-202.397,-132.525,0) rot=(0,0,1;0rad)
  shape: bbox 2.349 x 2.407 x 2e-07 mm, 0 faces, 0 solids (baked)
FEATURE [Part::Feature] path52401_7_8_1_1_7_3_6_7_6
  Placement = pos=(-197.397,-134.625,0) rot=(0,0,1;0rad)
  shape: bbox 2.349 x 2.407 x 2e-07 mm, 0 faces, 0 solids (baked)
FEATURE [Part::Feature] path52377_0_5_0_1_9_1_4_7_5
  Placement = pos=(-191.897,-128.725,0) rot=(0,0,1;0rad)
  shape: bbox 1.997 x 2.046 x 2e-07 mm, 0 faces, 0 solids (baked)
FEATURE [Part::Feature] path52456_0_5_2_2_2_7_4_6
  Placement = pos=(-197.397,-128.725,0) rot=(0,0,1;0rad)
  shape: bbox 4.029 x 4.128 x 2e-07 mm, 0 faces, 0 solids (baked)
FEATURE [Part::Feature] path61609_4_5_7_9_4_80_0_8_2_8_3
  shape: bbox 15.57 x 9.662 x 2e-07 mm, 0 faces, 0 solids (baked)
FEATURE [Part::Feature] path61609_4_5_7_9_4_80_0_8_2_8_3_6
  shape: bbox 16.06 x 7.248 x 2e-07 mm, 0 faces, 0 solids (baked)
FEATURE [Part::Feature] path61609_4_5_7_9_4_80_0_8_2_8_3_69
  shape: bbox 15.46 x 7.643 x 2e-07 mm, 0 faces, 0 solids (baked)
FEATURE [Part::Feature] path61609_4_5_7_9_4_80_0_8_2_8_3_7
  shape: bbox 14.99 x 9.16 x 2e-07 mm, 0 faces, 0 solids (baked)
FEATURE [Part::Extrusion] Extrude160
  Base = -> path52377_09_3_1_8_87_9
  Dir = (0,0,1)
  DirMode = 0
  FaceMakerClass = Part::FaceMakerBullseye
  LengthFwd = 2
  LengthRev = 0
  Solid = true
  Symmetric = false
FEATURE [Part::Extrusion] Extrude161
  Base = -> path52401_71_2_4_9_8_2
  Dir = (0,0,1)
  DirMode = 0
  FaceMakerClass = Part::FaceMakerBullseye
  LengthFwd = 2
  LengthRev = 0
  Solid = true
  Symmetric = false
FEATURE [Part::Extrusion] Extrude162
  Base = -> path52401_7_8_1_8_2_30_6
  Dir = (0,0,1)
  DirMode = 0
  FaceMakerClass = Part::FaceMakerBullseye
  LengthFwd = 2
  LengthRev = 0
  Solid = true
  Symmetric = false
FEATURE [Part::Extrusion] Extrude163
  Base = -> path52377_0_5_0_4_2_3_6
  Dir = (0,0,1)
  DirMode = 0
  FaceMakerClass = Part::FaceMakerBullseye
  LengthFwd = 2
  LengthRev = 0
  Solid = true
  Symmetric = false
FEATURE [Part::Extrusion] Extrude164
  Base = -> path52456_0_5_5_7_86_8
  Dir = (0,0,1)
  DirMode = 0
  FaceMakerClass = Part::FaceMakerBullseye
  LengthFwd = 2
  LengthRev = 0
  Solid = true
  Symmetric = false
FEATURE [Part::Extrusion] Extrude165
  Base = -> path52377_09_3_1_8_8_2_0
  Dir = (0,0,1)
  DirMode = 0
  FaceMakerClass = Part::FaceMakerBullseye
  LengthFwd = 2
  LengthRev = 0
  Solid = true
  Symmetric = false
FEATURE [Part::Extrusion] Extrude166
  Base = -> path52401_71_2_4_9_4_5_7
  Dir = (0,0,1)
  DirMode = 0
  FaceMakerClass = Part::FaceMakerBullseye
  LengthFwd = 2
  LengthRev = 0
  Solid = true
  Symmetric = false
FEATURE [Part::Extrusion] Extrude167
  Base = -> path52401_7_8_1_8_2_3_11_7
  Dir = (0,0,1)
  DirMode = 0
  FaceMakerClass = Part::FaceMakerBullseye
  LengthFwd = 2
  LengthRev = 0
  Solid = true
  Symmetric = false
FEATURE [Part::Extrusion] Extrude168
  Base = -> path52377_0_5_0_4_2_4_5_9
  Dir = (0,0,1)
  DirMode = 0
  FaceMakerClass = Part::FaceMakerBullseye
  LengthFwd = 2
  LengthRev = 0
  Solid = true
  Symmetric = false
FEATURE [Part::Extrusion] Extrude169
  Base = -> path52456_0_5_5_7_7_0_9
  Dir = (0,0,1)
  DirMode = 0
  FaceMakerClass = Part::FaceMakerBullseye
  LengthFwd = 2
  LengthRev = 0
  Solid = true
  Symmetric = false
FEATURE [Part::Extrusion] Extrude170
  Base = -> path52377_09_3_1_8_2_3_2
  Dir = (0,0,1)
  DirMode = 0
  FaceMakerClass = Part::FaceMakerBullseye
  LengthFwd = 2
  LengthRev = 0
  Solid = true
  Symmetric = false
FEATURE [Part::Extrusion] Extrude171
  Base = -> path52401_71_2_4_9_2_39_0
  Dir = (0,0,1)
  DirMode = 0
  FaceMakerClass = Part::FaceMakerBullseye
  LengthFwd = 2
  LengthRev = 0
  Solid = true
  Symmetric = false
FEATURE [Part::Extrusion] Extrude172
  Base = -> path52401_7_8_1_8_2_31_2_2
  Dir = (0,0,1)
  DirMode = 0
  FaceMakerClass = Part::FaceMakerBullseye
  LengthFwd = 2
  LengthRev = 0
  Solid = true
  Symmetric = false
FEATURE [Part::Extrusion] Extrude173
  Base = -> path52377_0_5_0_4_2_41_1_6
  Dir = (0,0,1)
  DirMode = 0
  FaceMakerClass = Part::FaceMakerBullseye
  LengthFwd = 2
  LengthRev = 0
  Solid = true
  Symmetric = false
FEATURE [Part::Extrusion] Extrude174
  Base = -> path52456_0_5_5_7_4_2_7
  Dir = (0,0,1)
  DirMode = 0
  FaceMakerClass = Part::FaceMakerBullseye
  LengthFwd = 2
  LengthRev = 0
  Solid = true
  Symmetric = false
FEATURE [Part::Extrusion] Extrude175
  Base = -> path52377_09_3_1_8_2_4_7_4
  Dir = (0,0,1)
  DirMode = 0
  FaceMakerClass = Part::FaceMakerBullseye
  LengthFwd = 2
  LengthRev = 0
  Solid = true
  Symmetric = false
FEATURE [Part::Extrusion] Extrude176
  Base = -> path52401_71_2_4_9_2_9_8_3
  Dir = (0,0,1)
  DirMode = 0
  FaceMakerClass = Part::FaceMakerBullseye
  LengthFwd = 2
  LengthRev = 0
  Solid = true
  Symmetric = false
FEATURE [Part::Extrusion] Extrude177
  Base = -> path52401_7_8_1_8_2_31_5_4_3
  Dir = (0,0,1)
  DirMode = 0
  FaceMakerClass = Part::FaceMakerBullseye
  LengthFwd = 2
  LengthRev = 0
  Solid = true
  Symmetric = false
FEATURE [Part::Extrusion] Extrude178
  Base = -> path52377_0_5_0_4_2_41_0_0_8
  Dir = (0,0,1)
  DirMode = 0
  FaceMakerClass = Part::FaceMakerBullseye
  LengthFwd = 2
  LengthRev = 0
  Solid = true
  Symmetric = false
FEATURE [Part::Extrusion] Extrude179
  Base = -> path52456_0_5_5_7_4_4_1_2
  Dir = (0,0,1)
  DirMode = 0
  FaceMakerClass = Part::FaceMakerBullseye
  LengthFwd = 2
  LengthRev = 0
  Solid = true
  Symmetric = false
FEATURE [Part::Extrusion] Extrude180
  Base = -> path52377_09_3_1_8_8_0_3_5
  Dir = (0,0,1)
  DirMode = 0
  FaceMakerClass = Part::FaceMakerBullseye
  LengthFwd = 2
  LengthRev = 0
  Solid = true
  Symmetric = false
FEATURE [Part::Extrusion] Extrude181
  Base = -> path52401_71_2_4_9_4_2_0_8
  Dir = (0,0,1)
  DirMode = 0
  FaceMakerClass = Part::FaceMakerBullseye
  LengthFwd = 2
  LengthRev = 0
  Solid = true
  Symmetric = false
FEATURE [Part::Extrusion] Extrude182
  Base = -> path52401_7_8_1_8_2_3_5_0_1
  Dir = (0,0,1)
  DirMode = 0
  FaceMakerClass = Part::FaceMakerBullseye
  LengthFwd = 2
  LengthRev = 0
  Solid = true
  Symmetric = false
FEATURE [Part::Extrusion] Extrude183
  Base = -> path52377_0_5_0_4_2_4_4_3_3
  Dir = (0,0,1)
  DirMode = 0
  FaceMakerClass = Part::FaceMakerBullseye
  LengthFwd = 2
  LengthRev = 0
  Solid = true
  Symmetric = false
FEATURE [Part::Extrusion] Extrude184
  Base = -> path52456_0_5_5_7_7_7_7_4
  Dir = (0,0,1)
  DirMode = 0
  FaceMakerClass = Part::FaceMakerBullseye
  LengthFwd = 2
  LengthRev = 0
  Solid = true
  Symmetric = false
FEATURE [Part::Extrusion] Extrude185
  Base = -> path52377_09_3_1_8_2_9_7_8
  Dir = (0,0,1)
  DirMode = 0
  FaceMakerClass = Part::FaceMakerBullseye
  LengthFwd = 2
  LengthRev = 0
  Solid = true
  Symmetric = false
FEATURE [Part::Extrusion] Extrude186
  Base = -> path52401_71_2_4_9_2_6_0_6
  Dir = (0,0,1)
  DirMode = 0
  FaceMakerClass = Part::FaceMakerBullseye
  LengthFwd = 2
  LengthRev = 0
  Solid = true
  Symmetric = false
FEATURE [Part::Extrusion] Extrude187
  Base = -> path52401_7_8_1_8_2_31_56_74_0
  Dir = (0,0,1)
  DirMode = 0
  FaceMakerClass = Part::FaceMakerBullseye
  LengthFwd = 2
  LengthRev = 0
  Solid = true
  Symmetric = false
FEATURE [Part::Extrusion] Extrude188
  Base = -> path52377_0_5_0_4_2_41_4_91_1
  Dir = (0,0,1)
  DirMode = 0
  FaceMakerClass = Part::FaceMakerBullseye
  LengthFwd = 2
  LengthRev = 0
  Solid = true
  Symmetric = false
FEATURE [Part::Extrusion] Extrude189
  Base = -> path52456_0_5_5_7_4_40_0_2
  Dir = (0,0,1)
  DirMode = 0
  FaceMakerClass = Part::FaceMakerBullseye
  LengthFwd = 2
  LengthRev = 0
  Solid = true
  Symmetric = false
FEATURE [Part::Extrusion] Extrude190
  Base = -> path52377_09_3_1_8_2_4_0_1_3
  Dir = (0,0,1)
  DirMode = 0
  FaceMakerClass = Part::FaceMakerBullseye
  LengthFwd = 2
  LengthRev = 0
  Solid = true
  Symmetric = false
FEATURE [Part::Extrusion] Extrude191
  Base = -> path52401_71_2_4_9_2_9_9_55_5
  Dir = (0,0,1)
  DirMode = 0
  FaceMakerClass = Part::FaceMakerBullseye
  LengthFwd = 2
  LengthRev = 0
  Solid = true
  Symmetric = false
FEATURE [Part::Extrusion] Extrude192
  Base = -> path52401_7_8_1_8_2_31_5_9_4_8
  Dir = (0,0,1)
  DirMode = 0
  FaceMakerClass = Part::FaceMakerBullseye
  LengthFwd = 2
  LengthRev = 0
  Solid = true
  Symmetric = false
FEATURE [Part::Extrusion] Extrude193
  Base = -> path52377_0_5_0_4_2_41_0_4_8_5
  Dir = (0,0,1)
  DirMode = 0
  FaceMakerClass = Part::FaceMakerBullseye
  LengthFwd = 2
  LengthRev = 0
  Solid = true
  Symmetric = false
FEATURE [Part::Extrusion] Extrude194
  Base = -> path52456_0_5_5_7_4_4_8_02_7
  Dir = (0,0,1)
  DirMode = 0
  FaceMakerClass = Part::FaceMakerBullseye
  LengthFwd = 2
  LengthRev = 0
  Solid = true
  Symmetric = false
FEATURE [Part::Extrusion] Extrude195
  Base = -> path52377_09_3_1_8_8_0_4_7_0
  Dir = (0,0,1)
  DirMode = 0
  FaceMakerClass = Part::FaceMakerBullseye
  LengthFwd = 2
  LengthRev = 0
  Solid = true
  Symmetric = false
FEATURE [Part::Extrusion] Extrude196
  Base = -> path52401_71_2_4_9_4_2_2_1_9
  Dir = (0,0,1)
  DirMode = 0
  FaceMakerClass = Part::FaceMakerBullseye
  LengthFwd = 2
  LengthRev = 0
  Solid = true
  Symmetric = false
FEATURE [Part::Extrusion] Extrude197
  Base = -> path52401_7_8_1_8_2_3_5_3_8_2
  Dir = (0,0,1)
  DirMode = 0
  FaceMakerClass = Part::FaceMakerBullseye
  LengthFwd = 2
  LengthRev = 0
  Solid = true
  Symmetric = false
FEATURE [Part::Extrusion] Extrude198
  Base = -> path52377_0_5_0_4_2_4_4_8_3_2
  Dir = (0,0,1)
  DirMode = 0
  FaceMakerClass = Part::FaceMakerBullseye
  LengthFwd = 2
  LengthRev = 0
  Solid = true
  Symmetric = false
FEATURE [Part::Extrusion] Extrude199
  Base = -> path52456_0_5_5_7_7_7_1_3_6
  Dir = (0,0,1)
  DirMode = 0
  FaceMakerClass = Part::FaceMakerBullseye
  LengthFwd = 2
  LengthRev = 0
  Solid = true
  Symmetric = false
FEATURE [Part::Extrusion] Extrude200
  Base = -> path52377_09_3_1_8_2_9_5_3_6
  Dir = (0,0,1)
  DirMode = 0
  FaceMakerClass = Part::FaceMakerBullseye
  LengthFwd = 2
  LengthRev = 0
  Solid = true
  Symmetric = false
FEATURE [Part::Extrusion] Extrude201
  Base = -> path52401_71_2_4_9_2_6_3_64_9
  Dir = (0,0,1)
  DirMode = 0
  FaceMakerClass = Part::FaceMakerBullseye
  LengthFwd = 2
  LengthRev = 0
  Solid = true
  Symmetric = false
FEATURE [Part::Extrusion] Extrude202
  Base = -> path52401_7_8_1_8_2_31_56_1_9_8
  Dir = (0,0,1)
  DirMode = 0
  FaceMakerClass = Part::FaceMakerBullseye
  LengthFwd = 2
  LengthRev = 0
  Solid = true
  Symmetric = false
FEATURE [Part::Extrusion] Extrude203
  Base = -> path52377_0_5_0_4_2_41_4_8_1_3
  Dir = (0,0,1)
  DirMode = 0
  FaceMakerClass = Part::FaceMakerBullseye
  LengthFwd = 2
  LengthRev = 0
  Solid = true
  Symmetric = false
FEATURE [Part::Extrusion] Extrude204
  Base = -> path52456_0_5_5_7_4_40_5_0_6
  Dir = (0,0,1)
  DirMode = 0
  FaceMakerClass = Part::FaceMakerBullseye
  LengthFwd = 2
  LengthRev = 0
  Solid = true
  Symmetric = false
FEATURE [Part::Extrusion] Extrude205
  Base = -> path52377_09_3_1_8_2_4_0_5_8_4
  Dir = (0,0,1)
  DirMode = 0
  FaceMakerClass = Part::FaceMakerBullseye
  LengthFwd = 2
  LengthRev = 0
  Solid = true
  Symmetric = false
FEATURE [Part::Extrusion] Extrude206
  Base = -> path52401_71_2_4_9_2_9_9_5_64_7
  Dir = (0,0,1)
  DirMode = 0
  FaceMakerClass = Part::FaceMakerBullseye
  LengthFwd = 2
  LengthRev = 0
  Solid = true
  Symmetric = false
FEATURE [Part::Extrusion] Extrude207
  Base = -> path52401_7_8_1_8_2_31_5_9_9_9_3
  Dir = (0,0,1)
  DirMode = 0
  FaceMakerClass = Part::FaceMakerBullseye
  LengthFwd = 2
  LengthRev = 0
  Solid = true
  Symmetric = false
FEATURE [Part::Extrusion] Extrude208
  Base = -> path52377_0_5_0_4_2_41_0_4_1_4_0
  Dir = (0,0,1)
  DirMode = 0
  FaceMakerClass = Part::FaceMakerBullseye
  LengthFwd = 2
  LengthRev = 0
  Solid = true
  Symmetric = false
FEATURE [Part::Extrusion] Extrude209
  Base = -> path52456_0_5_5_7_4_4_8_5_4_4
  Dir = (0,0,1)
  DirMode = 0
  FaceMakerClass = Part::FaceMakerBullseye
  LengthFwd = 2
  LengthRev = 0
  Solid = true
  Symmetric = false
FEATURE [Part::Extrusion] Extrude210
  Base = -> path52377_09_3_1_8_8_0_4_5_6_9
  Dir = (0,0,1)
  DirMode = 0
  FaceMakerClass = Part::FaceMakerBullseye
  LengthFwd = 2
  LengthRev = 0
  Solid = true
  Symmetric = false
FEATURE [Part::Extrusion] Extrude211
  Base = -> path52401_71_2_4_9_4_2_2_8_5_1
  Dir = (0,0,1)
  DirMode = 0
  FaceMakerClass = Part::FaceMakerBullseye
  LengthFwd = 2
  LengthRev = 0
  Solid = true
  Symmetric = false
FEATURE [Part::Extrusion] Extrude212
  Base = -> path52401_7_8_1_8_2_3_5_3_4_2_3
  Dir = (0,0,1)
  DirMode = 0
  FaceMakerClass = Part::FaceMakerBullseye
  LengthFwd = 2
  LengthRev = 0
  Solid = true
  Symmetric = false
FEATURE [Part::Extrusion] Extrude213
  Base = -> path52377_0_5_0_4_2_4_4_8_9_1_6
  Dir = (0,0,1)
  DirMode = 0
  FaceMakerClass = Part::FaceMakerBullseye
  LengthFwd = 2
  LengthRev = 0
  Solid = true
  Symmetric = false
FEATURE [Part::Extrusion] Extrude214
  Base = -> path52456_0_5_5_7_7_7_1_7_8_9
  Dir = (0,0,1)
  DirMode = 0
  FaceMakerClass = Part::FaceMakerBullseye
  LengthFwd = 2
  LengthRev = 0
  Solid = true
  Symmetric = false
FEATURE [Part::Extrusion] Extrude215
  Base = -> path52377_09_3_1_8_2_9_5_4_8_4
  Dir = (0,0,1)
  DirMode = 0
  FaceMakerClass = Part::FaceMakerBullseye
  LengthFwd = 2
  LengthRev = 0
  Solid = true
  Symmetric = false
FEATURE [Part::Extrusion] Extrude216
  Base = -> path52401_71_2_4_9_2_6_3_6_9_9
  Dir = (0,0,1)
  DirMode = 0
  FaceMakerClass = Part::FaceMakerBullseye
  LengthFwd = 2
  LengthRev = 0
  Solid = true
  Symmetric = false
FEATURE [Part::Extrusion] Extrude217
  Base = -> path52401_7_8_1_8_2_31_56_1_3_7_7
  Dir = (0,0,1)
  DirMode = 0
  FaceMakerClass = Part::FaceMakerBullseye
  LengthFwd = 2
  LengthRev = 0
  Solid = true
  Symmetric = false
FEATURE [Part::Extrusion] Extrude218
  Base = -> path52377_0_5_0_4_2_41_4_8_8_6_8
  Dir = (0,0,1)
  DirMode = 0
  FaceMakerClass = Part::FaceMakerBullseye
  LengthFwd = 2
  LengthRev = 0
  Solid = true
  Symmetric = false
FEATURE [Part::Extrusion] Extrude219
  Base = -> path52456_0_5_5_7_4_40_5_1_45_0
  Dir = (0,0,1)
  DirMode = 0
  FaceMakerClass = Part::FaceMakerBullseye
  LengthFwd = 2
  LengthRev = 0
  Solid = true
  Symmetric = false
FEATURE [Part::Extrusion] Extrude220
  Base = -> path52377_09_3_1_8_2_4_0_5_0_4_8
  Dir = (0,0,1)
  DirMode = 0
  FaceMakerClass = Part::FaceMakerBullseye
  LengthFwd = 2
  LengthRev = 0
  Solid = true
  Symmetric = false
FEATURE [Part::Extrusion] Extrude221
  Base = -> path52401_71_2_4_9_2_9_9_5_6_8_4
  Dir = (0,0,1)
  DirMode = 0
  FaceMakerClass = Part::FaceMakerBullseye
  LengthFwd = 2
  LengthRev = 0
  Solid = true
  Symmetric = false
FEATURE [Part::Extrusion] Extrude222
  Base = -> path52401_7_8_1_8_2_31_5_9_9_0_0_2
  Dir = (0,0,1)
  DirMode = 0
  FaceMakerClass = Part::FaceMakerBullseye
  LengthFwd = 2
  LengthRev = 0
  Solid = true
  Symmetric = false
FEATURE [Part::Extrusion] Extrude223
  Base = -> path52377_0_5_0_4_2_41_0_4_1_8_44_4
  Dir = (0,0,1)
  DirMode = 0
  FaceMakerClass = Part::FaceMakerBullseye
  LengthFwd = 2
  LengthRev = 0
  Solid = true
  Symmetric = false
FEATURE [Part::Extrusion] Extrude224
  Base = -> path52456_0_5_5_7_4_4_8_5_8_8_3
  Dir = (0,0,1)
  DirMode = 0
  FaceMakerClass = Part::FaceMakerBullseye
  LengthFwd = 2
  LengthRev = 0
  Solid = true
  Symmetric = false
FEATURE [Part::Extrusion] Extrude225
  Base = -> path52377_09_3_1_8_8_0_4_5_8_91_9
  Dir = (0,0,1)
  DirMode = 0
  FaceMakerClass = Part::FaceMakerBullseye
  LengthFwd = 2
  LengthRev = 0
  Solid = true
  Symmetric = false
FEATURE [Part::Extrusion] Extrude226
  Base = -> path52401_71_2_4_9_4_2_2_8_7_5_0
  Dir = (0,0,1)
  DirMode = 0
  FaceMakerClass = Part::FaceMakerBullseye
  LengthFwd = 2
  LengthRev = 0
  Solid = true
  Symmetric = false
FEATURE [Part::Extrusion] Extrude227
  Base = -> path52401_7_8_1_8_2_3_5_3_4_4_44_4
  Dir = (0,0,1)
  DirMode = 0
  FaceMakerClass = Part::FaceMakerBullseye
  LengthFwd = 2
  LengthRev = 0
  Solid = true
  Symmetric = false
FEATURE [Part::Extrusion] Extrude228
  Base = -> path52377_0_5_0_4_2_4_4_8_9_2_9_3
  Dir = (0,0,1)
  DirMode = 0
  FaceMakerClass = Part::FaceMakerBullseye
  LengthFwd = 2
  LengthRev = 0
  Solid = true
  Symmetric = false
FEATURE [Part::Extrusion] Extrude229
  Base = -> path52456_0_5_5_7_7_7_1_7_0_2_7
  Dir = (0,0,1)
  DirMode = 0
  FaceMakerClass = Part::FaceMakerBullseye
  LengthFwd = 2
  LengthRev = 0
  Solid = true
  Symmetric = false
FEATURE [Part::Extrusion] Extrude230
  Base = -> path52377_09_3_1_8_2_9_5_4_9_5_7
  Dir = (0,0,1)
  DirMode = 0
  FaceMakerClass = Part::FaceMakerBullseye
  LengthFwd = 2
  LengthRev = 0
  Solid = true
  Symmetric = false
FEATURE [Part::Extrusion] Extrude231
  Base = -> path52401_71_2_4_9_2_6_3_6_8_5_8
  Dir = (0,0,1)
  DirMode = 0
  FaceMakerClass = Part::FaceMakerBullseye
  LengthFwd = 2
  LengthRev = 0
  Solid = true
  Symmetric = false
FEATURE [Part::Extrusion] Extrude232
  Base = -> path52401_7_8_1_8_2_31_56_1_3_0_2_9
  Dir = (0,0,1)
  DirMode = 0
  FaceMakerClass = Part::FaceMakerBullseye
  LengthFwd = 2
  LengthRev = 0
  Solid = true
  Symmetric = false
FEATURE [Part::Extrusion] Extrude233
  Base = -> path52377_0_5_0_4_2_41_4_8_8_0_5_5
  Dir = (0,0,1)
  DirMode = 0
  FaceMakerClass = Part::FaceMakerBullseye
  LengthFwd = 2
  LengthRev = 0
  Solid = true
  Symmetric = false
FEATURE [Part::Extrusion] Extrude234
  Base = -> path52456_0_5_5_7_4_40_5_1_5_56_6
  Dir = (0,0,1)
  DirMode = 0
  FaceMakerClass = Part::FaceMakerBullseye
  LengthFwd = 2
  LengthRev = 0
  Solid = true
  Symmetric = false
FEATURE [Part::Extrusion] Extrude235
  Base = -> path52377_09_3_1_8_2_4_0_5_0_2_7_9
  Dir = (0,0,1)
  DirMode = 0
  FaceMakerClass = Part::FaceMakerBullseye
  LengthFwd = 2
  LengthRev = 0
  Solid = true
  Symmetric = false
FEATURE [Part::Extrusion] Extrude236
  Base = -> path52401_71_2_4_9_2_9_9_5_6_2_6_5
  Dir = (0,0,1)
  DirMode = 0
  FaceMakerClass = Part::FaceMakerBullseye
  LengthFwd = 2
  LengthRev = 0
  Solid = true
  Symmetric = false
FEATURE [Part::Extrusion] Extrude237
  Base = -> path52401_7_8_1_8_2_31_5_9_9_0_7_2_4
  Dir = (0,0,1)
  DirMode = 0
  FaceMakerClass = Part::FaceMakerBullseye
  LengthFwd = 2
  LengthRev = 0
  Solid = true
  Symmetric = false
FEATURE [Part::Extrusion] Extrude238
  Base = -> path52377_0_5_0_4_2_41_0_4_1_8_4_4_5
  Dir = (0,0,1)
  DirMode = 0
  FaceMakerClass = Part::FaceMakerBullseye
  LengthFwd = 2
  LengthRev = 0
  Solid = true
  Symmetric = false
FEATURE [Part::Extrusion] Extrude239
  Base = -> path52456_0_5_5_7_4_4_8_5_8_0_3_1
  Dir = (0,0,1)
  DirMode = 0
  FaceMakerClass = Part::FaceMakerBullseye
  LengthFwd = 2
  LengthRev = 0
  Solid = true
  Symmetric = false
FEATURE [Part::Extrusion] Extrude240
  Base = -> path52377_09_3_1_8_8_0_4_5_8_9_1_3
  Dir = (0,0,1)
  DirMode = 0
  FaceMakerClass = Part::FaceMakerBullseye
  LengthFwd = 2
  LengthRev = 0
  Solid = true
  Symmetric = false
FEATURE [Part::Extrusion] Extrude241
  Base = -> path52401_71_2_4_9_4_2_2_8_7_6_2_4
  Dir = (0,0,1)
  DirMode = 0
  FaceMakerClass = Part::FaceMakerBullseye
  LengthFwd = 2
  LengthRev = 0
  Solid = true
  Symmetric = false
FEATURE [Part::Extrusion] Extrude242
  Base = -> path52401_7_8_1_8_2_3_5_3_4_4_8_8_9
  Dir = (0,0,1)
  DirMode = 0
  FaceMakerClass = Part::FaceMakerBullseye
  LengthFwd = 2
  LengthRev = 0
  Solid = true
  Symmetric = false
FEATURE [Part::Extrusion] Extrude243
  Base = -> path52377_0_5_0_4_2_4_4_8_9_2_0_5_5
  Dir = (0,0,1)
  DirMode = 0
  FaceMakerClass = Part::FaceMakerBullseye
  LengthFwd = 2
  LengthRev = 0
  Solid = true
  Symmetric = false
FEATURE [Part::Extrusion] Extrude244
  Base = -> path52456_0_5_5_7_7_7_1_7_0_0_6_4
  Dir = (0,0,1)
  DirMode = 0
  FaceMakerClass = Part::FaceMakerBullseye
  LengthFwd = 2
  LengthRev = 0
  Solid = true
  Symmetric = false
FEATURE [Part::Extrusion] Extrude245
  Base = -> path37937_8_6
  Dir = (0,0,1)
  DirMode = 0
  FaceMakerClass = Part::FaceMakerBullseye
  LengthFwd = 2
  LengthRev = 0
  Solid = true
  Symmetric = false
FEATURE [Part::Extrusion] Extrude246
  Base = -> path37931_6_7
  Dir = (0,0,1)
  DirMode = 0
  FaceMakerClass = Part::FaceMakerBullseye
  LengthFwd = 2
  LengthRev = 0
  Solid = true
  Symmetric = false
FEATURE [Part::Extrusion] Extrude247
  Base = -> path37321_9_5
  Dir = (0,0,1)
  DirMode = 0
  FaceMakerClass = Part::FaceMakerBullseye
  LengthFwd = 2
  LengthRev = 0
  Solid = true
  Symmetric = false
FEATURE [Part::Extrusion] Extrude248
  Base = -> path37327_3_6
  Dir = (0,0,1)
  DirMode = 0
  FaceMakerClass = Part::FaceMakerBullseye
  LengthFwd = 2
  LengthRev = 0
  Solid = true
  Symmetric = false
FEATURE [Part::Extrusion] Extrude249
  Base = -> path37329_6_1
  Dir = (0,0,1)
  DirMode = 0
  FaceMakerClass = Part::FaceMakerBullseye
  LengthFwd = 2
  LengthRev = 0
  Solid = true
  Symmetric = false
FEATURE [Part::Extrusion] Extrude250
  Base = -> path37333_00_0
  Dir = (0,0,1)
  DirMode = 0
  FaceMakerClass = Part::FaceMakerBullseye
  LengthFwd = 2
  LengthRev = 0
  Solid = true
  Symmetric = false
FEATURE [Part::Extrusion] Extrude251
  Base = -> circle37301_1_8
  Dir = (0,0,1)
  DirMode = 0
  FaceMakerClass = Part::FaceMakerBullseye
  LengthFwd = 2
  LengthRev = 0
  Solid = true
  Symmetric = false
FEATURE [Part::Extrusion] Extrude252
  Base = -> circle37295_7_4
  Dir = (0,0,1)
  DirMode = 0
  FaceMakerClass = Part::FaceMakerBullseye
  LengthFwd = 2
  LengthRev = 0
  Solid = true
  Symmetric = false
FEATURE [Part::Extrusion] Extrude253
  Base = -> rect117948_11_2
  Dir = (0,0,1)
  DirMode = 0
  FaceMakerClass = Part::FaceMakerBullseye
  LengthFwd = 2
  LengthRev = 0
  Solid = true
  Symmetric = false
FEATURE [Part::Extrusion] Extrude254
  Base = -> rect117948_2_00_4
  Dir = (0,0,1)
  DirMode = 0
  FaceMakerClass = Part::FaceMakerBullseye
  LengthFwd = 2
  LengthRev = 0
  Solid = true
  Symmetric = false
FEATURE [Part::Extrusion] Extrude255
  Base = -> path61609_4_5_7_9_4_80_0_4
  Dir = (0,0,1)
  DirMode = 0
  FaceMakerClass = Part::FaceMakerBullseye
  LengthFwd = 2
  LengthRev = 0
  Solid = true
  Symmetric = false
FEATURE [Part::Extrusion] Extrude256
  Base = -> path61609_4_5_7_9_4_80_0_3_84
  Dir = (0,0,1)
  DirMode = 0
  FaceMakerClass = Part::FaceMakerBullseye
  LengthFwd = 2
  LengthRev = 0
  Solid = true
  Symmetric = false
FEATURE [Part::Extrusion] Extrude257
  Base = -> path61609_4_5_7_9_4_80_0_8_5
  Dir = (0,0,1)
  DirMode = 0
  FaceMakerClass = Part::FaceMakerBullseye
  LengthFwd = 2
  LengthRev = 0
  Solid = true
  Symmetric = false
FEATURE [Part::Extrusion] Extrude258
  Base = -> path61609_4_5_7_9_4_80_0_3_8_08
  Dir = (0,0,1)
  DirMode = 0
  FaceMakerClass = Part::FaceMakerBullseye
  LengthFwd = 2
  LengthRev = 0
  Solid = true
  Symmetric = false
FEATURE [Part::Extrusion] Extrude259
  Base = -> path61609_4_5_7_9_4_80_0_3_8_6_37
  Dir = (0,0,1)
  DirMode = 0
  FaceMakerClass = Part::FaceMakerBullseye
  LengthFwd = 2
  LengthRev = 0
  Solid = true
  Symmetric = false
FEATURE [Part::Extrusion] Extrude260
  Base = -> path61609_4_5_7_9_4_80_0_8_3_4
  Dir = (0,0,1)
  DirMode = 0
  FaceMakerClass = Part::FaceMakerBullseye
  LengthFwd = 2
  LengthRev = 0
  Solid = true
  Symmetric = false
FEATURE [Part::Extrusion] Extrude261
  Base = -> path61609_4_5_7_9_4_80_0_3_8_9_8
  Dir = (0,0,1)
  DirMode = 0
  FaceMakerClass = Part::FaceMakerBullseye
  LengthFwd = 2
  LengthRev = 0
  Solid = true
  Symmetric = false
FEATURE [Part::Extrusion] Extrude262
  Base = -> path61609_4_5_7_9_4_80_0_3_8_6_1_7
  Dir = (0,0,1)
  DirMode = 0
  FaceMakerClass = Part::FaceMakerBullseye
  LengthFwd = 2
  LengthRev = 0
  Solid = true
  Symmetric = false
FEATURE [Part::Extrusion] Extrude263
  Base = -> path61609_4_5_7_9_4_80_0_8_7_4
  Dir = (0,0,1)
  DirMode = 0
  FaceMakerClass = Part::FaceMakerBullseye
  LengthFwd = 2
  LengthRev = 0
  Solid = true
  Symmetric = false
FEATURE [Part::Extrusion] Extrude264
  Base = -> path61609_4_5_7_9_4_80_0_3_8_91_7
  Dir = (0,0,1)
  DirMode = 0
  FaceMakerClass = Part::FaceMakerBullseye
  LengthFwd = 2
  LengthRev = 0
  Solid = true
  Symmetric = false
FEATURE [Part::Extrusion] Extrude265
  Base = -> path61609_4_5_7_9_4_80_0_3_8_6_3_5
  Dir = (0,0,1)
  DirMode = 0
  FaceMakerClass = Part::FaceMakerBullseye
  LengthFwd = 2
  LengthRev = 0
  Solid = true
  Symmetric = false
FEATURE [Part::Extrusion] Extrude266
  Base = -> path61609_4_5_7_9_4_80_0_8_8_0
  Dir = (0,0,1)
  DirMode = 0
  FaceMakerClass = Part::FaceMakerBullseye
  LengthFwd = 2
  LengthRev = 0
  Solid = true
  Symmetric = false
FEATURE [Part::Extrusion] Extrude267
  Base = -> path61609_4_5_7_9_4_80_0_3_8_0_5
  Dir = (0,0,1)
  DirMode = 0
  FaceMakerClass = Part::FaceMakerBullseye
  LengthFwd = 2
  LengthRev = 0
  Solid = true
  Symmetric = false
FEATURE [Part::Extrusion] Extrude268
  Base = -> path61609_4_5_7_9_4_80_0_3_8_6_7_1
  Dir = (0,0,1)
  DirMode = 0
  FaceMakerClass = Part::FaceMakerBullseye
  LengthFwd = 2
  LengthRev = 0
  Solid = true
  Symmetric = false
FEATURE [Part::Extrusion] Extrude269
  Base = -> path61609_4_5_7_9_4_80_0_8_2_8
  Dir = (0,0,1)
  DirMode = 0
  FaceMakerClass = Part::FaceMakerBullseye
  LengthFwd = 2
  LengthRev = 0
  Solid = true
  Symmetric = false
FEATURE [Part::Extrusion] Extrude270
  Base = -> path61609_4_5_7_9_4_80_0_3_8_60_1
  Dir = (0,0,1)
  DirMode = 0
  FaceMakerClass = Part::FaceMakerBullseye
  LengthFwd = 2
  LengthRev = 0
  Solid = true
  Symmetric = false
FEATURE [Part::Extrusion] Extrude271
  Base = -> path61609_4_5_7_9_4_80_0_3_8_6_4_3
  Dir = (0,0,1)
  DirMode = 0
  FaceMakerClass = Part::FaceMakerBullseye
  LengthFwd = 2
  LengthRev = 0
  Solid = true
  Symmetric = false
FEATURE [Part::Extrusion] Extrude272
  Base = -> path52377_09_3_5_7_6_7_3
  Dir = (0,0,1)
  DirMode = 0
  FaceMakerClass = Part::FaceMakerBullseye
  LengthFwd = 2
  LengthRev = 0
  Solid = true
  Symmetric = false
FEATURE [Part::Extrusion] Extrude273
  Base = -> path52401_71_2_5_9_2_77_3
  Dir = (0,0,1)
  DirMode = 0
  FaceMakerClass = Part::FaceMakerBullseye
  LengthFwd = 2
  LengthRev = 0
  Solid = true
  Symmetric = false
FEATURE [Part::Extrusion] Extrude274
  Base = -> path52401_7_8_1_1_7_3_9_0
  Dir = (0,0,1)
  DirMode = 0
  FaceMakerClass = Part::FaceMakerBullseye
  LengthFwd = 2
  LengthRev = 0
  Solid = true
  Symmetric = false
FEATURE [Part::Extrusion] Extrude275
  Base = -> path52377_0_5_0_1_9_1_5_5
  Dir = (0,0,1)
  DirMode = 0
  FaceMakerClass = Part::FaceMakerBullseye
  LengthFwd = 2
  LengthRev = 0
  Solid = true
  Symmetric = false
FEATURE [Part::Extrusion] Extrude276
  Base = -> path52456_0_5_2_2_2_3_5
  Dir = (0,0,1)
  DirMode = 0
  FaceMakerClass = Part::FaceMakerBullseye
  LengthFwd = 2
  LengthRev = 0
  Solid = true
  Symmetric = false
FEATURE [Part::Extrusion] Extrude277
  Base = -> path52377_09_3_5_7_6_0_0_2
  Dir = (0,0,1)
  DirMode = 0
  FaceMakerClass = Part::FaceMakerBullseye
  LengthFwd = 2
  LengthRev = 0
  Solid = true
  Symmetric = false
FEATURE [Part::Extrusion] Extrude278
  Base = -> path52401_71_2_5_9_2_7_5_4
  Dir = (0,0,1)
  DirMode = 0
  FaceMakerClass = Part::FaceMakerBullseye
  LengthFwd = 2
  LengthRev = 0
  Solid = true
  Symmetric = false
FEATURE [Part::Extrusion] Extrude279
  Base = -> path52401_7_8_1_1_7_3_8_4_4
  Dir = (0,0,1)
  DirMode = 0
  FaceMakerClass = Part::FaceMakerBullseye
  LengthFwd = 2
  LengthRev = 0
  Solid = true
  Symmetric = false
FEATURE [Part::Extrusion] Extrude280
  Base = -> path52377_0_5_0_1_9_1_0_6_9
  Dir = (0,0,1)
  DirMode = 0
  FaceMakerClass = Part::FaceMakerBullseye
  LengthFwd = 2
  LengthRev = 0
  Solid = true
  Symmetric = false
FEATURE [Part::Extrusion] Extrude281
  Base = -> path52456_0_5_2_2_2_9_9_3
  Dir = (0,0,1)
  DirMode = 0
  FaceMakerClass = Part::FaceMakerBullseye
  LengthFwd = 2
  LengthRev = 0
  Solid = true
  Symmetric = false
FEATURE [Part::Extrusion] Extrude282
  Base = -> path52377_09_3_5_7_6_6_7_9
  Dir = (0,0,1)
  DirMode = 0
  FaceMakerClass = Part::FaceMakerBullseye
  LengthFwd = 2
  LengthRev = 0
  Solid = true
  Symmetric = false
FEATURE [Part::Extrusion] Extrude283
  Base = -> path52401_71_2_5_9_2_1_4_5
  Dir = (0,0,1)
  DirMode = 0
  FaceMakerClass = Part::FaceMakerBullseye
  LengthFwd = 2
  LengthRev = 0
  Solid = true
  Symmetric = false
FEATURE [Part::Extrusion] Extrude284
  Base = -> path52401_7_8_1_1_7_3_1_9_1
  Dir = (0,0,1)
  DirMode = 0
  FaceMakerClass = Part::FaceMakerBullseye
  LengthFwd = 2
  LengthRev = 0
  Solid = true
  Symmetric = false
FEATURE [Part::Extrusion] Extrude285
  Base = -> path52377_0_5_0_1_9_1_3_9_3
  Dir = (0,0,1)
  DirMode = 0
  FaceMakerClass = Part::FaceMakerBullseye
  LengthFwd = 2
  LengthRev = 0
  Solid = true
  Symmetric = false
FEATURE [Part::Extrusion] Extrude286
  Base = -> path52456_0_5_2_2_2_5_8_5
  Dir = (0,0,1)
  DirMode = 0
  FaceMakerClass = Part::FaceMakerBullseye
  LengthFwd = 2
  LengthRev = 0
  Solid = true
  Symmetric = false
FEATURE [Part::Extrusion] Extrude287
  Base = -> path52377_09_3_5_7_6_4_7_2
  Dir = (0,0,1)
  DirMode = 0
  FaceMakerClass = Part::FaceMakerBullseye
  LengthFwd = 2
  LengthRev = 0
  Solid = true
  Symmetric = false
FEATURE [Part::Extrusion] Extrude288
  Base = -> path52401_71_2_5_9_2_8_0_6
  Dir = (0,0,1)
  DirMode = 0
  FaceMakerClass = Part::FaceMakerBullseye
  LengthFwd = 2
  LengthRev = 0
  Solid = true
  Symmetric = false
FEATURE [Part::Extrusion] Extrude289
  Base = -> path52401_7_8_1_1_7_3_6_7_6
  Dir = (0,0,1)
  DirMode = 0
  FaceMakerClass = Part::FaceMakerBullseye
  LengthFwd = 2
  LengthRev = 0
  Solid = true
  Symmetric = false
FEATURE [Part::Extrusion] Extrude290
  Base = -> path52377_0_5_0_1_9_1_4_7_5
  Dir = (0,0,1)
  DirMode = 0
  FaceMakerClass = Part::FaceMakerBullseye
  LengthFwd = 2
  LengthRev = 0
  Solid = true
  Symmetric = false
FEATURE [Part::Extrusion] Extrude291
  Base = -> path52456_0_5_2_2_2_7_4_6
  Dir = (0,0,1)
  DirMode = 0
  FaceMakerClass = Part::FaceMakerBullseye
  LengthFwd = 2
  LengthRev = 0
  Solid = true
  Symmetric = false
FEATURE [Part::Extrusion] Extrude292
  Base = -> path61609_4_5_7_9_4_80_0_8_2_8_3
  Dir = (0,0,1)
  DirMode = 0
  FaceMakerClass = Part::FaceMakerBullseye
  LengthFwd = 2
  LengthRev = 0
  Solid = true
  Symmetric = false
FEATURE [Part::Extrusion] Extrude293
  Base = -> path61609_4_5_7_9_4_80_0_8_2_8_3_6
  Dir = (0,0,1)
  DirMode = 0
  FaceMakerClass = Part::FaceMakerBullseye
  LengthFwd = 2
  LengthRev = 0
  Solid = true
  Symmetric = false
FEATURE [Part::Extrusion] Extrude294
  Base = -> path61609_4_5_7_9_4_80_0_8_2_8_3_69
  Dir = (0,0,1)
  DirMode = 0
  FaceMakerClass = Part::FaceMakerBullseye
  LengthFwd = 2
  LengthRev = 0
  Solid = true
  Symmetric = false
FEATURE [Part::Extrusion] Extrude295
  Base = -> path61609_4_5_7_9_4_80_0_8_2_8_3_7
  Dir = (0,0,1)
  DirMode = 0
  FaceMakerClass = Part::FaceMakerBullseye
  LengthFwd = 2
  LengthRev = 0
  Solid = true
  Symmetric = false
FEATURE [Part::MultiFuse] Fusion003  label="wells_right"
  Placement = pos=(0,0,1) rot=(0,0,1;0rad)
  Shapes = -> [Extrude295,Extrude160,Extrude161,Extrude162,Extrude163,Extrude164,Extrude165,Extrude166,Extrude167,Extrude168,Extrude169,Extrude170,Extrude171,Extrude172,Extrude173,Extrude174,Extrude175,Extrude176,Extrude177,Extrude178,Extrude179,Extrude180,Extrude181,Extrude182,Extrude183,Extrude184,Extrude185,Extrude186,Extrude187,Extrude188,Extrude189,Extrude190,Extrude191,Extrude192,Extrude193,Extrude194,+100 more]
FEATURE [Part::FeaturePython] XOR001  label="right"  # WARN: FeaturePython — macro-defined, semantics opaque (R4)
  Objects = -> [Fusion003,Extrude148,Extrude149,Fusion002]
  Tolerance = 0
FEATURE [Part::Mirroring] Part__Mirroring  label="right (Mirror #1)"
  Base = (0,0,0)
  Normal = (1,0,0)
  Placement = pos=(140,90,0) rot=(0,0,1;0rad)
  Source = -> XOR001
